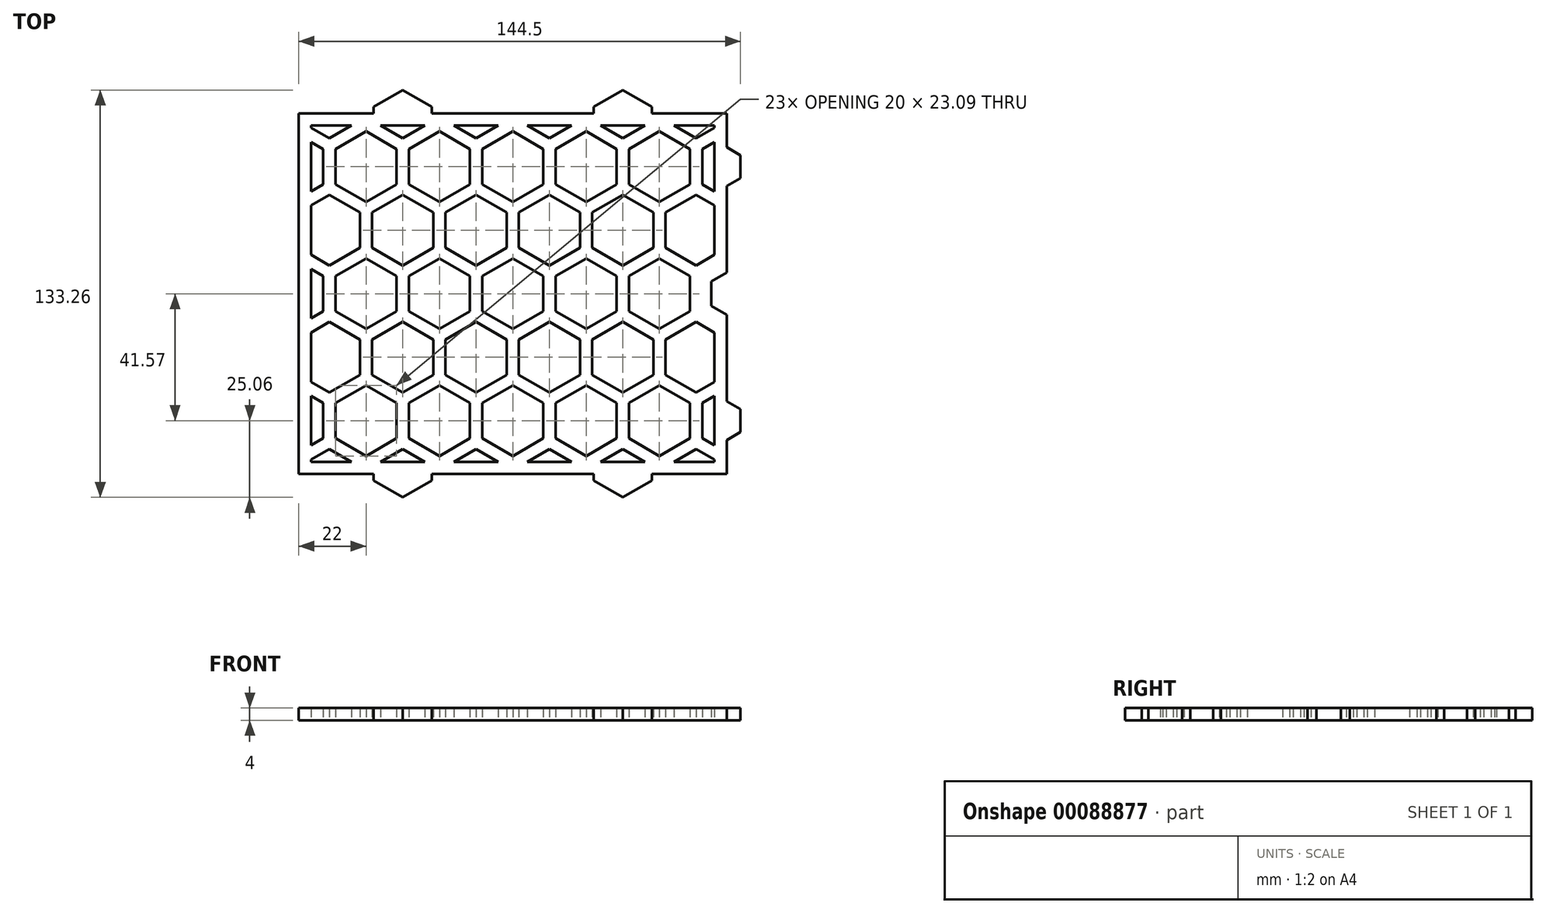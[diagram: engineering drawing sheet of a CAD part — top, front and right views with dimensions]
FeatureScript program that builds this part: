
annotation { "Feature Type Name" : "Feature", "Feature Type Description" : "" }
export const myFeature = defineFeature(function(context is Context, id is Id, definition is map)
    precondition{}
    {
        {
            var Q0;
            Q0=qCreatedBy(makeId("Top.planeOp"),FACE);
            var sketch = newSketch(context, id + "F0", { "sketchPlane" : qUnion([Q0])});
            skLineSegment(sketch, "E0.bottom", {"start": v(70, -59) * mm, "end": v(-70, -59) * mm});
            skLineSegment(sketch, "E0.top", {"start": v(70, 59) * mm, "end": v(-70, 59) * mm});
            skLineSegment(sketch, "E0.left", {"start": v(70, -59) * mm, "end": v(70, 59) * mm});
            skLineSegment(sketch, "E0.right", {"start": v(-70, -59) * mm, "end": v(-70, 59) * mm});
            skPoint(sketch, "E0.middle", {"position": v(0, 0) * mm});
            skLineSegment(sketch, "E1.0", {"start": v(-66, -55) * mm, "end": v(-66, 55) * mm});
            skLineSegment(sketch, "E1.1", {"start": v(66, -55) * mm, "end": v(-66, -55) * mm});
            skLineSegment(sketch, "E1.2", {"start": v(66, -55) * mm, "end": v(66, 55) * mm});
            skLineSegment(sketch, "E1.3", {"start": v(66, 55) * mm, "end": v(-66, 55) * mm});
            skSolve(sketch);
        }
        {
            var Q0;
            Q0=qSketchRegion(id+"F0",true);
            extrude(context, id + "F1", {"entities" : qUnion([Q0]), "depth" : 4 * mm});
        }
        {
            var Q0;
            Q0=qCreatedBy(makeId("Top.planeOp"),FACE);
            var sketch = newSketch(context, id + "F2", { "sketchPlane" : qUnion([Q0])});
            skLineSegment(sketch, "E2.0.1.1", {"start": v(-62, -47.34) * mm, "end": v(-66, -49.65) * mm});
            skLineSegment(sketch, "E2.0.1.5", {"start": v(-66, -33.49) * mm, "end": v(-62, -35.8) * mm});
            skLineSegment(sketch, "E2.0.1.13", {"start": v(-62, -35.8) * mm, "end": v(-62, -47.34) * mm});
            skLineSegment(sketch, "E2.0.2.1", {"start": v(-62, -5.77) * mm, "end": v(-66, -8.08) * mm});
            skLineSegment(sketch, "E2.0.2.5", {"start": v(-66, 8.08) * mm, "end": v(-62, 5.77) * mm});
            skLineSegment(sketch, "E2.0.2.13", {"start": v(-62, 5.77) * mm, "end": v(-62, -5.77) * mm});
            skLineSegment(sketch, "E2.0.3.1", {"start": v(-62, 35.8) * mm, "end": v(-66, 33.49) * mm});
            skLineSegment(sketch, "E2.0.3.5", {"start": v(-66, 49.65) * mm, "end": v(-62, 47.34) * mm});
            skLineSegment(sketch, "E2.0.3.13", {"start": v(-62, 47.34) * mm, "end": v(-62, 35.8) * mm});
            skLineSegment(sketch, "E2.1.0.7", {"start": v(-60, -50.8) * mm, "end": v(-52.74, -55) * mm});
            skLineSegment(sketch, "E2.1.0.8", {"start": v(-66, -54.27) * mm, "end": v(-60, -50.8) * mm});
            skCircle(sketch, "E2.1.1.0", {"center": v(-48, -41.57) * mm, "radius": 11.55 * mm, "construction": true});
            skLineSegment(sketch, "E2.1.1.1", {"start": v(-38, -47.34) * mm, "end": v(-48, -53.12) * mm});
            skLineSegment(sketch, "E2.1.1.2", {"start": v(-48, -53.12) * mm, "end": v(-58, -47.34) * mm});
            skLineSegment(sketch, "E2.1.1.3", {"start": v(-58, -47.34) * mm, "end": v(-58, -35.8) * mm});
            skLineSegment(sketch, "E2.1.1.4", {"start": v(-58, -35.8) * mm, "end": v(-48, -30.02) * mm});
            skLineSegment(sketch, "E2.1.1.5", {"start": v(-48, -30.02) * mm, "end": v(-38, -35.8) * mm});
            skLineSegment(sketch, "E2.1.1.6", {"start": v(-50, -15.01) * mm, "end": v(-50, -26.56) * mm});
            skLineSegment(sketch, "E2.1.1.7", {"start": v(-60, -9.24) * mm, "end": v(-50, -15.01) * mm});
            skLineSegment(sketch, "E2.1.1.8", {"start": v(-66, -12.7) * mm, "end": v(-60, -9.24) * mm});
            skLineSegment(sketch, "E2.1.1.10", {"start": v(-60, -32.33) * mm, "end": v(-66, -28.87) * mm});
            skLineSegment(sketch, "E2.1.1.11", {"start": v(-50, -26.56) * mm, "end": v(-60, -32.33) * mm});
            skLineSegment(sketch, "E2.1.1.13", {"start": v(-38, -35.8) * mm, "end": v(-38, -47.34) * mm});
            skCircle(sketch, "E2.1.2.0", {"center": v(-48, 0) * mm, "radius": 11.55 * mm, "construction": true});
            skLineSegment(sketch, "E2.1.2.1", {"start": v(-38, -5.77) * mm, "end": v(-48, -11.55) * mm});
            skLineSegment(sketch, "E2.1.2.2", {"start": v(-48, -11.55) * mm, "end": v(-58, -5.77) * mm});
            skLineSegment(sketch, "E2.1.2.3", {"start": v(-58, -5.77) * mm, "end": v(-58, 5.77) * mm});
            skLineSegment(sketch, "E2.1.2.4", {"start": v(-58, 5.77) * mm, "end": v(-48, 11.55) * mm});
            skLineSegment(sketch, "E2.1.2.5", {"start": v(-48, 11.55) * mm, "end": v(-38, 5.77) * mm});
            skLineSegment(sketch, "E2.1.2.6", {"start": v(-50, 26.56) * mm, "end": v(-50, 15.01) * mm});
            skLineSegment(sketch, "E2.1.2.7", {"start": v(-60, 32.33) * mm, "end": v(-50, 26.56) * mm});
            skLineSegment(sketch, "E2.1.2.8", {"start": v(-66, 28.87) * mm, "end": v(-60, 32.33) * mm});
            skLineSegment(sketch, "E2.1.2.10", {"start": v(-60, 9.24) * mm, "end": v(-66, 12.7) * mm});
            skLineSegment(sketch, "E2.1.2.11", {"start": v(-50, 15.01) * mm, "end": v(-60, 9.24) * mm});
            skLineSegment(sketch, "E2.1.2.13", {"start": v(-38, 5.77) * mm, "end": v(-38, -5.77) * mm});
            skCircle(sketch, "E2.1.3.0", {"center": v(-48, 41.57) * mm, "radius": 11.55 * mm, "construction": true});
            skLineSegment(sketch, "E2.1.3.1", {"start": v(-38, 35.8) * mm, "end": v(-48, 30.02) * mm});
            skLineSegment(sketch, "E2.1.3.2", {"start": v(-48, 30.02) * mm, "end": v(-58, 35.8) * mm});
            skLineSegment(sketch, "E2.1.3.3", {"start": v(-58, 35.8) * mm, "end": v(-58, 47.34) * mm});
            skLineSegment(sketch, "E2.1.3.4", {"start": v(-58, 47.34) * mm, "end": v(-48, 53.12) * mm});
            skLineSegment(sketch, "E2.1.3.5", {"start": v(-48, 53.12) * mm, "end": v(-38, 47.34) * mm});
            skLineSegment(sketch, "E2.1.3.10", {"start": v(-60, 50.8) * mm, "end": v(-66, 54.27) * mm});
            skLineSegment(sketch, "E2.1.3.11", {"start": v(-52.74, 55) * mm, "end": v(-60, 50.8) * mm});
            skLineSegment(sketch, "E2.1.3.13", {"start": v(-38, 47.34) * mm, "end": v(-38, 35.8) * mm});
            skLineSegment(sketch, "E2.2.0.7", {"start": v(-36, -50.8) * mm, "end": v(-28.74, -55) * mm});
            skLineSegment(sketch, "E2.2.0.8", {"start": v(-43.26, -55) * mm, "end": v(-36, -50.8) * mm});
            skCircle(sketch, "E2.2.1.0", {"center": v(-24, -41.57) * mm, "radius": 11.55 * mm, "construction": true});
            skLineSegment(sketch, "E2.2.1.1", {"start": v(-14, -47.34) * mm, "end": v(-24, -53.12) * mm});
            skLineSegment(sketch, "E2.2.1.2", {"start": v(-24, -53.12) * mm, "end": v(-34, -47.34) * mm});
            skLineSegment(sketch, "E2.2.1.3", {"start": v(-34, -47.34) * mm, "end": v(-34, -35.8) * mm});
            skLineSegment(sketch, "E2.2.1.4", {"start": v(-34, -35.8) * mm, "end": v(-24, -30.02) * mm});
            skLineSegment(sketch, "E2.2.1.5", {"start": v(-24, -30.02) * mm, "end": v(-14, -35.8) * mm});
            skLineSegment(sketch, "E2.2.1.6", {"start": v(-26, -15.01) * mm, "end": v(-26, -26.56) * mm});
            skLineSegment(sketch, "E2.2.1.7", {"start": v(-36, -9.24) * mm, "end": v(-26, -15.01) * mm});
            skLineSegment(sketch, "E2.2.1.8", {"start": v(-46, -15.01) * mm, "end": v(-36, -9.24) * mm});
            skLineSegment(sketch, "E2.2.1.9", {"start": v(-46, -26.56) * mm, "end": v(-46, -15.01) * mm});
            skLineSegment(sketch, "E2.2.1.10", {"start": v(-36, -32.33) * mm, "end": v(-46, -26.56) * mm});
            skLineSegment(sketch, "E2.2.1.11", {"start": v(-26, -26.56) * mm, "end": v(-36, -32.33) * mm});
            skCircle(sketch, "E2.2.1.12", {"center": v(-36, -20.79) * mm, "radius": 11.55 * mm, "construction": true});
            skLineSegment(sketch, "E2.2.1.13", {"start": v(-14, -35.8) * mm, "end": v(-14, -47.34) * mm});
            skCircle(sketch, "E2.2.2.0", {"center": v(-24, 0) * mm, "radius": 11.55 * mm, "construction": true});
            skLineSegment(sketch, "E2.2.2.1", {"start": v(-14, -5.77) * mm, "end": v(-24, -11.55) * mm});
            skLineSegment(sketch, "E2.2.2.2", {"start": v(-24, -11.55) * mm, "end": v(-34, -5.77) * mm});
            skLineSegment(sketch, "E2.2.2.3", {"start": v(-34, -5.77) * mm, "end": v(-34, 5.77) * mm});
            skLineSegment(sketch, "E2.2.2.4", {"start": v(-34, 5.77) * mm, "end": v(-24, 11.55) * mm});
            skLineSegment(sketch, "E2.2.2.5", {"start": v(-24, 11.55) * mm, "end": v(-14, 5.77) * mm});
            skLineSegment(sketch, "E2.2.2.6", {"start": v(-26, 26.56) * mm, "end": v(-26, 15.01) * mm});
            skLineSegment(sketch, "E2.2.2.7", {"start": v(-36, 32.33) * mm, "end": v(-26, 26.56) * mm});
            skLineSegment(sketch, "E2.2.2.8", {"start": v(-46, 26.56) * mm, "end": v(-36, 32.33) * mm});
            skLineSegment(sketch, "E2.2.2.9", {"start": v(-46, 15.01) * mm, "end": v(-46, 26.56) * mm});
            skLineSegment(sketch, "E2.2.2.10", {"start": v(-36, 9.24) * mm, "end": v(-46, 15.01) * mm});
            skLineSegment(sketch, "E2.2.2.11", {"start": v(-26, 15.01) * mm, "end": v(-36, 9.24) * mm});
            skCircle(sketch, "E2.2.2.12", {"center": v(-36, 20.78) * mm, "radius": 11.55 * mm, "construction": true});
            skLineSegment(sketch, "E2.2.2.13", {"start": v(-14, 5.77) * mm, "end": v(-14, -5.77) * mm});
            skCircle(sketch, "E2.2.3.0", {"center": v(-24, 41.57) * mm, "radius": 11.55 * mm, "construction": true});
            skLineSegment(sketch, "E2.2.3.1", {"start": v(-14, 35.8) * mm, "end": v(-24, 30.02) * mm});
            skLineSegment(sketch, "E2.2.3.2", {"start": v(-24, 30.02) * mm, "end": v(-34, 35.8) * mm});
            skLineSegment(sketch, "E2.2.3.3", {"start": v(-34, 35.8) * mm, "end": v(-34, 47.34) * mm});
            skLineSegment(sketch, "E2.2.3.4", {"start": v(-34, 47.34) * mm, "end": v(-24, 53.12) * mm});
            skLineSegment(sketch, "E2.2.3.5", {"start": v(-24, 53.12) * mm, "end": v(-14, 47.34) * mm});
            skLineSegment(sketch, "E2.2.3.10", {"start": v(-36, 50.8) * mm, "end": v(-43.26, 55) * mm});
            skLineSegment(sketch, "E2.2.3.11", {"start": v(-28.74, 55) * mm, "end": v(-36, 50.8) * mm});
            skLineSegment(sketch, "E2.2.3.13", {"start": v(-14, 47.34) * mm, "end": v(-14, 35.8) * mm});
            skLineSegment(sketch, "E2.3.0.7", {"start": v(-12, -50.8) * mm, "end": v(-4.74, -55) * mm});
            skLineSegment(sketch, "E2.3.0.8", {"start": v(-19.26, -55) * mm, "end": v(-12, -50.8) * mm});
            skCircle(sketch, "E2.3.1.0", {"center": v(0, -41.57) * mm, "radius": 11.55 * mm, "construction": true});
            skLineSegment(sketch, "E2.3.1.1", {"start": v(10, -47.34) * mm, "end": v(0, -53.12) * mm});
            skLineSegment(sketch, "E2.3.1.2", {"start": v(0, -53.12) * mm, "end": v(-10, -47.34) * mm});
            skLineSegment(sketch, "E2.3.1.3", {"start": v(-10, -47.34) * mm, "end": v(-10, -35.8) * mm});
            skLineSegment(sketch, "E2.3.1.4", {"start": v(-10, -35.8) * mm, "end": v(0, -30.02) * mm});
            skLineSegment(sketch, "E2.3.1.5", {"start": v(0, -30.02) * mm, "end": v(10, -35.8) * mm});
            skLineSegment(sketch, "E2.3.1.6", {"start": v(-2, -15.01) * mm, "end": v(-2, -26.56) * mm});
            skLineSegment(sketch, "E2.3.1.7", {"start": v(-12, -9.24) * mm, "end": v(-2, -15.01) * mm});
            skLineSegment(sketch, "E2.3.1.8", {"start": v(-22, -15.01) * mm, "end": v(-12, -9.24) * mm});
            skLineSegment(sketch, "E2.3.1.9", {"start": v(-22, -26.56) * mm, "end": v(-22, -15.01) * mm});
            skLineSegment(sketch, "E2.3.1.10", {"start": v(-12, -32.33) * mm, "end": v(-22, -26.56) * mm});
            skLineSegment(sketch, "E2.3.1.11", {"start": v(-2, -26.56) * mm, "end": v(-12, -32.33) * mm});
            skCircle(sketch, "E2.3.1.12", {"center": v(-12, -20.79) * mm, "radius": 11.55 * mm, "construction": true});
            skLineSegment(sketch, "E2.3.1.13", {"start": v(10, -35.8) * mm, "end": v(10, -47.34) * mm});
            skCircle(sketch, "E2.3.2.0", {"center": v(0, 0) * mm, "radius": 11.55 * mm, "construction": true});
            skLineSegment(sketch, "E2.3.2.1", {"start": v(10, -5.77) * mm, "end": v(0, -11.55) * mm});
            skLineSegment(sketch, "E2.3.2.2", {"start": v(0, -11.55) * mm, "end": v(-10, -5.77) * mm});
            skLineSegment(sketch, "E2.3.2.3", {"start": v(-10, -5.77) * mm, "end": v(-10, 5.77) * mm});
            skLineSegment(sketch, "E2.3.2.4", {"start": v(-10, 5.77) * mm, "end": v(0, 11.55) * mm});
            skLineSegment(sketch, "E2.3.2.5", {"start": v(0, 11.55) * mm, "end": v(10, 5.77) * mm});
            skLineSegment(sketch, "E2.3.2.6", {"start": v(-2, 26.56) * mm, "end": v(-2, 15.01) * mm});
            skLineSegment(sketch, "E2.3.2.7", {"start": v(-12, 32.33) * mm, "end": v(-2, 26.56) * mm});
            skLineSegment(sketch, "E2.3.2.8", {"start": v(-22, 26.56) * mm, "end": v(-12, 32.33) * mm});
            skLineSegment(sketch, "E2.3.2.9", {"start": v(-22, 15.01) * mm, "end": v(-22, 26.56) * mm});
            skLineSegment(sketch, "E2.3.2.10", {"start": v(-12, 9.24) * mm, "end": v(-22, 15.01) * mm});
            skLineSegment(sketch, "E2.3.2.11", {"start": v(-2, 15.01) * mm, "end": v(-12, 9.24) * mm});
            skCircle(sketch, "E2.3.2.12", {"center": v(-12, 20.78) * mm, "radius": 11.55 * mm, "construction": true});
            skLineSegment(sketch, "E2.3.2.13", {"start": v(10, 5.77) * mm, "end": v(10, -5.77) * mm});
            skCircle(sketch, "E2.3.3.0", {"center": v(0, 41.57) * mm, "radius": 11.55 * mm, "construction": true});
            skLineSegment(sketch, "E2.3.3.1", {"start": v(10, 35.8) * mm, "end": v(0, 30.02) * mm});
            skLineSegment(sketch, "E2.3.3.2", {"start": v(0, 30.02) * mm, "end": v(-10, 35.8) * mm});
            skLineSegment(sketch, "E2.3.3.3", {"start": v(-10, 35.8) * mm, "end": v(-10, 47.34) * mm});
            skLineSegment(sketch, "E2.3.3.4", {"start": v(-10, 47.34) * mm, "end": v(0, 53.12) * mm});
            skLineSegment(sketch, "E2.3.3.5", {"start": v(0, 53.12) * mm, "end": v(10, 47.34) * mm});
            skLineSegment(sketch, "E2.3.3.10", {"start": v(-12, 50.8) * mm, "end": v(-19.26, 55) * mm});
            skLineSegment(sketch, "E2.3.3.11", {"start": v(-4.74, 55) * mm, "end": v(-12, 50.8) * mm});
            skLineSegment(sketch, "E2.3.3.13", {"start": v(10, 47.34) * mm, "end": v(10, 35.8) * mm});
            skLineSegment(sketch, "E2.4.0.7", {"start": v(12, -50.8) * mm, "end": v(19.26, -55) * mm});
            skLineSegment(sketch, "E2.4.0.8", {"start": v(4.74, -55) * mm, "end": v(12, -50.8) * mm});
            skCircle(sketch, "E2.4.1.0", {"center": v(24, -41.57) * mm, "radius": 11.55 * mm, "construction": true});
            skLineSegment(sketch, "E2.4.1.1", {"start": v(34, -47.34) * mm, "end": v(24, -53.12) * mm});
            skLineSegment(sketch, "E2.4.1.2", {"start": v(24, -53.12) * mm, "end": v(14, -47.34) * mm});
            skLineSegment(sketch, "E2.4.1.3", {"start": v(14, -47.34) * mm, "end": v(14, -35.8) * mm});
            skLineSegment(sketch, "E2.4.1.4", {"start": v(14, -35.8) * mm, "end": v(24, -30.02) * mm});
            skLineSegment(sketch, "E2.4.1.5", {"start": v(24, -30.02) * mm, "end": v(34, -35.8) * mm});
            skLineSegment(sketch, "E2.4.1.6", {"start": v(22, -15.01) * mm, "end": v(22, -26.56) * mm});
            skLineSegment(sketch, "E2.4.1.7", {"start": v(12, -9.24) * mm, "end": v(22, -15.01) * mm});
            skLineSegment(sketch, "E2.4.1.8", {"start": v(2, -15.01) * mm, "end": v(12, -9.24) * mm});
            skLineSegment(sketch, "E2.4.1.9", {"start": v(2, -26.56) * mm, "end": v(2, -15.01) * mm});
            skLineSegment(sketch, "E2.4.1.10", {"start": v(12, -32.33) * mm, "end": v(2, -26.56) * mm});
            skLineSegment(sketch, "E2.4.1.11", {"start": v(22, -26.56) * mm, "end": v(12, -32.33) * mm});
            skCircle(sketch, "E2.4.1.12", {"center": v(12, -20.79) * mm, "radius": 11.55 * mm, "construction": true});
            skLineSegment(sketch, "E2.4.1.13", {"start": v(34, -35.8) * mm, "end": v(34, -47.34) * mm});
            skCircle(sketch, "E2.4.2.0", {"center": v(24, 0) * mm, "radius": 11.55 * mm, "construction": true});
            skLineSegment(sketch, "E2.4.2.1", {"start": v(34, -5.77) * mm, "end": v(24, -11.55) * mm});
            skLineSegment(sketch, "E2.4.2.2", {"start": v(24, -11.55) * mm, "end": v(14, -5.77) * mm});
            skLineSegment(sketch, "E2.4.2.3", {"start": v(14, -5.77) * mm, "end": v(14, 5.77) * mm});
            skLineSegment(sketch, "E2.4.2.4", {"start": v(14, 5.77) * mm, "end": v(24, 11.55) * mm});
            skLineSegment(sketch, "E2.4.2.5", {"start": v(24, 11.55) * mm, "end": v(34, 5.77) * mm});
            skLineSegment(sketch, "E2.4.2.6", {"start": v(22, 26.56) * mm, "end": v(22, 15.01) * mm});
            skLineSegment(sketch, "E2.4.2.7", {"start": v(12, 32.33) * mm, "end": v(22, 26.56) * mm});
            skLineSegment(sketch, "E2.4.2.8", {"start": v(2, 26.56) * mm, "end": v(12, 32.33) * mm});
            skLineSegment(sketch, "E2.4.2.9", {"start": v(2, 15.01) * mm, "end": v(2, 26.56) * mm});
            skLineSegment(sketch, "E2.4.2.10", {"start": v(12, 9.24) * mm, "end": v(2, 15.01) * mm});
            skLineSegment(sketch, "E2.4.2.11", {"start": v(22, 15.01) * mm, "end": v(12, 9.24) * mm});
            skCircle(sketch, "E2.4.2.12", {"center": v(12, 20.78) * mm, "radius": 11.55 * mm, "construction": true});
            skLineSegment(sketch, "E2.4.2.13", {"start": v(34, 5.77) * mm, "end": v(34, -5.77) * mm});
            skCircle(sketch, "E2.4.3.0", {"center": v(24, 41.57) * mm, "radius": 11.55 * mm, "construction": true});
            skLineSegment(sketch, "E2.4.3.1", {"start": v(34, 35.8) * mm, "end": v(24, 30.02) * mm});
            skLineSegment(sketch, "E2.4.3.2", {"start": v(24, 30.02) * mm, "end": v(14, 35.8) * mm});
            skLineSegment(sketch, "E2.4.3.3", {"start": v(14, 35.8) * mm, "end": v(14, 47.34) * mm});
            skLineSegment(sketch, "E2.4.3.4", {"start": v(14, 47.34) * mm, "end": v(24, 53.12) * mm});
            skLineSegment(sketch, "E2.4.3.5", {"start": v(24, 53.12) * mm, "end": v(34, 47.34) * mm});
            skLineSegment(sketch, "E2.4.3.10", {"start": v(12, 50.8) * mm, "end": v(4.74, 55) * mm});
            skLineSegment(sketch, "E2.4.3.11", {"start": v(19.26, 55) * mm, "end": v(12, 50.8) * mm});
            skLineSegment(sketch, "E2.4.3.13", {"start": v(34, 47.34) * mm, "end": v(34, 35.8) * mm});
            skLineSegment(sketch, "E2.5.0.7", {"start": v(36, -50.8) * mm, "end": v(43.26, -55) * mm});
            skLineSegment(sketch, "E2.5.0.8", {"start": v(28.74, -55) * mm, "end": v(36, -50.8) * mm});
            skCircle(sketch, "E2.5.1.0", {"center": v(48, -41.57) * mm, "radius": 11.55 * mm, "construction": true});
            skLineSegment(sketch, "E2.5.1.1", {"start": v(58, -47.34) * mm, "end": v(48, -53.12) * mm});
            skLineSegment(sketch, "E2.5.1.2", {"start": v(48, -53.12) * mm, "end": v(38, -47.34) * mm});
            skLineSegment(sketch, "E2.5.1.3", {"start": v(38, -47.34) * mm, "end": v(38, -35.8) * mm});
            skLineSegment(sketch, "E2.5.1.4", {"start": v(38, -35.8) * mm, "end": v(48, -30.02) * mm});
            skLineSegment(sketch, "E2.5.1.5", {"start": v(48, -30.02) * mm, "end": v(58, -35.8) * mm});
            skLineSegment(sketch, "E2.5.1.6", {"start": v(46, -15.01) * mm, "end": v(46, -26.56) * mm});
            skLineSegment(sketch, "E2.5.1.7", {"start": v(36, -9.24) * mm, "end": v(46, -15.01) * mm});
            skLineSegment(sketch, "E2.5.1.8", {"start": v(26, -15.01) * mm, "end": v(36, -9.24) * mm});
            skLineSegment(sketch, "E2.5.1.9", {"start": v(26, -26.56) * mm, "end": v(26, -15.01) * mm});
            skLineSegment(sketch, "E2.5.1.10", {"start": v(36, -32.33) * mm, "end": v(26, -26.56) * mm});
            skLineSegment(sketch, "E2.5.1.11", {"start": v(46, -26.56) * mm, "end": v(36, -32.33) * mm});
            skCircle(sketch, "E2.5.1.12", {"center": v(36, -20.79) * mm, "radius": 11.55 * mm, "construction": true});
            skLineSegment(sketch, "E2.5.1.13", {"start": v(58, -35.8) * mm, "end": v(58, -47.34) * mm});
            skCircle(sketch, "E2.5.2.0", {"center": v(48, 0) * mm, "radius": 11.55 * mm, "construction": true});
            skLineSegment(sketch, "E2.5.2.1", {"start": v(58, -5.77) * mm, "end": v(48, -11.55) * mm});
            skLineSegment(sketch, "E2.5.2.2", {"start": v(48, -11.55) * mm, "end": v(38, -5.77) * mm});
            skLineSegment(sketch, "E2.5.2.3", {"start": v(38, -5.77) * mm, "end": v(38, 5.77) * mm});
            skLineSegment(sketch, "E2.5.2.4", {"start": v(38, 5.77) * mm, "end": v(48, 11.55) * mm});
            skLineSegment(sketch, "E2.5.2.5", {"start": v(48, 11.55) * mm, "end": v(58, 5.77) * mm});
            skLineSegment(sketch, "E2.5.2.6", {"start": v(46, 26.56) * mm, "end": v(46, 15.01) * mm});
            skLineSegment(sketch, "E2.5.2.7", {"start": v(36, 32.33) * mm, "end": v(46, 26.56) * mm});
            skLineSegment(sketch, "E2.5.2.8", {"start": v(26, 26.56) * mm, "end": v(36, 32.33) * mm});
            skLineSegment(sketch, "E2.5.2.9", {"start": v(26, 15.01) * mm, "end": v(26, 26.56) * mm});
            skLineSegment(sketch, "E2.5.2.10", {"start": v(36, 9.24) * mm, "end": v(26, 15.01) * mm});
            skLineSegment(sketch, "E2.5.2.11", {"start": v(46, 15.01) * mm, "end": v(36, 9.24) * mm});
            skCircle(sketch, "E2.5.2.12", {"center": v(36, 20.78) * mm, "radius": 11.55 * mm, "construction": true});
            skLineSegment(sketch, "E2.5.2.13", {"start": v(58, 5.77) * mm, "end": v(58, -5.77) * mm});
            skCircle(sketch, "E2.5.3.0", {"center": v(48, 41.57) * mm, "radius": 11.55 * mm, "construction": true});
            skLineSegment(sketch, "E2.5.3.1", {"start": v(58, 35.8) * mm, "end": v(48, 30.02) * mm});
            skLineSegment(sketch, "E2.5.3.2", {"start": v(48, 30.02) * mm, "end": v(38, 35.8) * mm});
            skLineSegment(sketch, "E2.5.3.3", {"start": v(38, 35.8) * mm, "end": v(38, 47.34) * mm});
            skLineSegment(sketch, "E2.5.3.4", {"start": v(38, 47.34) * mm, "end": v(48, 53.12) * mm});
            skLineSegment(sketch, "E2.5.3.5", {"start": v(48, 53.12) * mm, "end": v(58, 47.34) * mm});
            skLineSegment(sketch, "E2.5.3.10", {"start": v(36, 50.8) * mm, "end": v(28.74, 55) * mm});
            skLineSegment(sketch, "E2.5.3.11", {"start": v(43.26, 55) * mm, "end": v(36, 50.8) * mm});
            skLineSegment(sketch, "E2.5.3.13", {"start": v(58, 47.34) * mm, "end": v(58, 35.8) * mm});
            skLineSegment(sketch, "E2.6.0.7", {"start": v(60, -50.8) * mm, "end": v(66, -54.27) * mm});
            skLineSegment(sketch, "E2.6.0.8", {"start": v(52.74, -55) * mm, "end": v(60, -50.8) * mm});
            skLineSegment(sketch, "E2.6.1.2", {"start": v(66, -49.65) * mm, "end": v(62, -47.34) * mm});
            skLineSegment(sketch, "E2.6.1.3", {"start": v(62, -47.34) * mm, "end": v(62, -35.8) * mm});
            skLineSegment(sketch, "E2.6.1.4", {"start": v(62, -35.8) * mm, "end": v(66, -33.49) * mm});
            skLineSegment(sketch, "E2.6.1.7", {"start": v(60, -9.24) * mm, "end": v(66, -12.7) * mm});
            skLineSegment(sketch, "E2.6.1.8", {"start": v(50, -15.01) * mm, "end": v(60, -9.24) * mm});
            skLineSegment(sketch, "E2.6.1.9", {"start": v(50, -26.56) * mm, "end": v(50, -15.01) * mm});
            skLineSegment(sketch, "E2.6.1.10", {"start": v(60, -32.33) * mm, "end": v(50, -26.56) * mm});
            skLineSegment(sketch, "E2.6.1.11", {"start": v(66, -28.87) * mm, "end": v(60, -32.33) * mm});
            skLineSegment(sketch, "E2.6.2.2", {"start": v(66, -8.08) * mm, "end": v(62, -5.77) * mm});
            skLineSegment(sketch, "E2.6.2.3", {"start": v(62, -5.77) * mm, "end": v(62, 5.77) * mm});
            skLineSegment(sketch, "E2.6.2.4", {"start": v(62, 5.77) * mm, "end": v(66, 8.08) * mm});
            skLineSegment(sketch, "E2.6.2.7", {"start": v(60, 32.33) * mm, "end": v(66, 28.87) * mm});
            skLineSegment(sketch, "E2.6.2.8", {"start": v(50, 26.56) * mm, "end": v(60, 32.33) * mm});
            skLineSegment(sketch, "E2.6.2.9", {"start": v(50, 15.01) * mm, "end": v(50, 26.56) * mm});
            skLineSegment(sketch, "E2.6.2.10", {"start": v(60, 9.24) * mm, "end": v(50, 15.01) * mm});
            skLineSegment(sketch, "E2.6.2.11", {"start": v(66, 12.7) * mm, "end": v(60, 9.24) * mm});
            skLineSegment(sketch, "E2.6.3.2", {"start": v(66, 33.49) * mm, "end": v(62, 35.8) * mm});
            skLineSegment(sketch, "E2.6.3.3", {"start": v(62, 35.8) * mm, "end": v(62, 47.34) * mm});
            skLineSegment(sketch, "E2.6.3.4", {"start": v(62, 47.34) * mm, "end": v(66, 49.65) * mm});
            skLineSegment(sketch, "E2.6.3.10", {"start": v(60, 50.8) * mm, "end": v(52.74, 55) * mm});
            skLineSegment(sketch, "E2.6.3.11", {"start": v(66, 54.27) * mm, "end": v(60, 50.8) * mm});
            skLineSegment(sketch, "E3.0", {"start": v(-66, -55) * mm, "end": v(-66, -54.27) * mm});
            skLineSegment(sketch, "E3.1", {"start": v(66, 55) * mm, "end": v(52.74, 55) * mm});
            skLineSegment(sketch, "E3.2", {"start": v(66, -55) * mm, "end": v(66, -54.27) * mm});
            skLineSegment(sketch, "E3.3", {"start": v(66, -55) * mm, "end": v(52.74, -55) * mm});
            skLineSegment(sketch, "E4.trimOffspring", {"start": v(-66, 54.27) * mm, "end": v(-66, 55) * mm});
            skLineSegment(sketch, "E5.trimOffspring", {"start": v(-66, 33.49) * mm, "end": v(-66, 49.65) * mm});
            skLineSegment(sketch, "E6.trimOffspring", {"start": v(-66, 12.7) * mm, "end": v(-66, 28.87) * mm});
            skLineSegment(sketch, "E7.trimOffspring", {"start": v(-52.74, 55) * mm, "end": v(-66, 55) * mm});
            skLineSegment(sketch, "E8.trimOffspring", {"start": v(-28.74, 55) * mm, "end": v(-43.26, 55) * mm});
            skLineSegment(sketch, "E9.trimOffspring", {"start": v(-4.74, 55) * mm, "end": v(-19.26, 55) * mm});
            skLineSegment(sketch, "E10.trimOffspring", {"start": v(19.26, 55) * mm, "end": v(4.74, 55) * mm});
            skLineSegment(sketch, "E11.trimOffspring", {"start": v(43.26, 55) * mm, "end": v(28.74, 55) * mm});
            skLineSegment(sketch, "E12.trimOffspring", {"start": v(66, 54.27) * mm, "end": v(66, 55) * mm});
            skLineSegment(sketch, "E13.trimOffspring", {"start": v(66, 33.49) * mm, "end": v(66, 49.65) * mm});
            skLineSegment(sketch, "E14.trimOffspring", {"start": v(66, 12.7) * mm, "end": v(66, 28.87) * mm});
            skLineSegment(sketch, "E15.trimOffspring", {"start": v(66, -8.08) * mm, "end": v(66, 8.08) * mm});
            skLineSegment(sketch, "E16.trimOffspring", {"start": v(66, -28.87) * mm, "end": v(66, -12.7) * mm});
            skLineSegment(sketch, "E17.trimOffspring", {"start": v(66, -49.65) * mm, "end": v(66, -33.49) * mm});
            skLineSegment(sketch, "E18.trimOffspring", {"start": v(43.26, -55) * mm, "end": v(28.74, -55) * mm});
            skLineSegment(sketch, "E19.trimOffspring", {"start": v(19.26, -55) * mm, "end": v(4.74, -55) * mm});
            skLineSegment(sketch, "E20.trimOffspring", {"start": v(-4.74, -55) * mm, "end": v(-19.26, -55) * mm});
            skLineSegment(sketch, "E21.trimOffspring", {"start": v(-28.74, -55) * mm, "end": v(-43.26, -55) * mm});
            skLineSegment(sketch, "E22.trimOffspring", {"start": v(-52.74, -55) * mm, "end": v(-66, -55) * mm});
            skLineSegment(sketch, "E23.trimOffspring", {"start": v(-66, -49.65) * mm, "end": v(-66, -33.49) * mm});
            skLineSegment(sketch, "E24.trimOffspring", {"start": v(-66, -28.87) * mm, "end": v(-66, -12.7) * mm});
            skLineSegment(sketch, "E25.trimOffspring", {"start": v(-66, -8.08) * mm, "end": v(-66, 8.08) * mm});
            skLineSegment(sketch, "E26.0", {"start": v(-70, -59) * mm, "end": v(-70, 59) * mm});
            skLineSegment(sketch, "E26.1", {"start": v(70, 59) * mm, "end": v(-70, 59) * mm});
            skLineSegment(sketch, "E26.2", {"start": v(70, -59) * mm, "end": v(70, 59) * mm});
            skLineSegment(sketch, "E26.3", {"start": v(70, -59) * mm, "end": v(-70, -59) * mm});
            skSolve(sketch);
        }
        {
            var Q0;
            Q0=qSketchRegion(id+"F2",true);
            var Q1;
            Q1=makeQuery(id+"F1.opExtrude","CAP_FACE",FACE,{"disambiguationData":[OSD([sQuery(id+"F0.wireOp",EDGE,"E0.bottom"),sQuery(id+"F0.wireOp",EDGE,"E0.top"),sQuery(id+"F0.wireOp",EDGE,"E0.left"),sQuery(id+"F0.wireOp",EDGE,"E0.right"),sQuery(id+"F0.wireOp",EDGE,"E1.0"),sQuery(id+"F0.wireOp",EDGE,"E1.1"),sQuery(id+"F0.wireOp",EDGE,"E1.2"),sQuery(id+"F0.wireOp",EDGE,"E1.3")])],"isStart":false});
            extrude(context, id + "F3", {"entities" : qUnion([Q0]), "operationType" : NewBodyOperationType.ADD, "endBound" : BoundingType.UP_TO_SURFACE, "endBoundEntityFace" : qUnion([Q1]), "depth" : 4 * mm});
        }
        {
            var Q0;
            Q0=qCreatedBy(makeId("Top.planeOp"),FACE);
            var sketch = newSketch(context, id + "F4", { "sketchPlane" : qUnion([Q0])});
            skCircle(sketch, "E27.cCircle", {"center": v(68, 41.57) * mm, "radius": 11.55 * mm, "construction": true});
            skLineSegment(sketch, "E27.0", {"start": v(78, 35.8) * mm, "end": v(70, 31.18) * mm, "construction": true});
            skLineSegment(sketch, "E27.4", {"start": v(70, 51.96) * mm, "end": v(78, 47.34) * mm, "construction": true});
            skLineSegment(sketch, "E27.5", {"start": v(78, 47.34) * mm, "end": v(78, 35.8) * mm, "construction": true});
            skCircle(sketch, "E28.cCircle", {"center": v(68, -41.57) * mm, "radius": 11.55 * mm, "construction": true});
            skLineSegment(sketch, "E28.3", {"start": v(70, -31.18) * mm, "end": v(78, -35.8) * mm, "construction": true});
            skLineSegment(sketch, "E28.4", {"start": v(78, -35.8) * mm, "end": v(78, -47.34) * mm, "construction": true});
            skLineSegment(sketch, "E28.5", {"start": v(78, -47.34) * mm, "end": v(70, -51.96) * mm, "construction": true});
            skLineSegment(sketch, "E29.0", {"start": v(70, -59) * mm, "end": v(70, 59) * mm});
            skPoint(sketch, "E30.orphan", {"position": v(68, -30.02) * mm});
            skLineSegment(sketch, "E31.0", {"start": v(74.5, 37.82) * mm, "end": v(68.25, 34.2) * mm});
            skLineSegment(sketch, "E31.1", {"start": v(74.5, 45.32) * mm, "end": v(74.5, 37.82) * mm});
            skLineSegment(sketch, "E31.2", {"start": v(68.25, 48.93) * mm, "end": v(74.5, 45.32) * mm});
            skLineSegment(sketch, "E32.0", {"start": v(74.5, -45.32) * mm, "end": v(68.25, -48.93) * mm});
            skLineSegment(sketch, "E32.1", {"start": v(74.5, -37.82) * mm, "end": v(74.5, -45.32) * mm});
            skLineSegment(sketch, "E32.2", {"start": v(68.25, -34.2) * mm, "end": v(74.5, -37.82) * mm});
            skSolve(sketch);
        }
        {
            var Q0;
            Q0=qSketchRegion(id+"F4",true);
            var Q1;
            Q1=makeQuery(id+"F3.boolean.opBoolean","MERGE",FACE,{"derivedFrom":[makeQuery(id+"F1.opExtrude","CAP_FACE",FACE,{"disambiguationData":[OSD([sQuery(id+"F0.wireOp",EDGE,"E0.bottom"),sQuery(id+"F0.wireOp",EDGE,"E0.top"),sQuery(id+"F0.wireOp",EDGE,"E0.left"),sQuery(id+"F0.wireOp",EDGE,"E0.right"),sQuery(id+"F0.wireOp",EDGE,"E1.0"),sQuery(id+"F0.wireOp",EDGE,"E1.1"),sQuery(id+"F0.wireOp",EDGE,"E1.2"),sQuery(id+"F0.wireOp",EDGE,"E1.3")])],"isStart":false}),makeQuery(id+"F3.opExtrude","CAP_FACE",FACE,{"disambiguationData":[OSD([sQuery(id+"F2.wireOp",EDGE,"E2.0.1.1"),sQuery(id+"F2.wireOp",EDGE,"E2.0.1.5"),sQuery(id+"F2.wireOp",EDGE,"E2.0.1.13"),sQuery(id+"F2.wireOp",EDGE,"E2.0.2.1"),sQuery(id+"F2.wireOp",EDGE,"E2.0.2.5"),sQuery(id+"F2.wireOp",EDGE,"E2.0.2.13"),sQuery(id+"F2.wireOp",EDGE,"E2.0.3.1"),sQuery(id+"F2.wireOp",EDGE,"E2.0.3.5"),sQuery(id+"F2.wireOp",EDGE,"E2.0.3.13"),sQuery(id+"F2.wireOp",EDGE,"E2.1.0.7"),sQuery(id+"F2.wireOp",EDGE,"E2.1.0.8"),sQuery(id+"F2.wireOp",EDGE,"E2.1.1.1"),sQuery(id+"F2.wireOp",EDGE,"E2.1.1.2"),sQuery(id+"F2.wireOp",EDGE,"E2.1.1.3"),sQuery(id+"F2.wireOp",EDGE,"E2.1.1.4"),sQuery(id+"F2.wireOp",EDGE,"E2.1.1.5"),sQuery(id+"F2.wireOp",EDGE,"E2.1.1.6"),sQuery(id+"F2.wireOp",EDGE,"E2.1.1.7"),sQuery(id+"F2.wireOp",EDGE,"E2.1.1.8"),sQuery(id+"F2.wireOp",EDGE,"E2.1.1.10"),sQuery(id+"F2.wireOp",EDGE,"E2.1.1.11"),sQuery(id+"F2.wireOp",EDGE,"E2.1.1.13"),sQuery(id+"F2.wireOp",EDGE,"E2.1.2.1"),sQuery(id+"F2.wireOp",EDGE,"E2.1.2.2"),sQuery(id+"F2.wireOp",EDGE,"E2.1.2.3"),sQuery(id+"F2.wireOp",EDGE,"E2.1.2.4"),sQuery(id+"F2.wireOp",EDGE,"E2.1.2.5"),sQuery(id+"F2.wireOp",EDGE,"E2.1.2.6"),sQuery(id+"F2.wireOp",EDGE,"E2.1.2.7"),sQuery(id+"F2.wireOp",EDGE,"E2.1.2.8"),sQuery(id+"F2.wireOp",EDGE,"E2.1.2.10"),sQuery(id+"F2.wireOp",EDGE,"E2.1.2.11"),sQuery(id+"F2.wireOp",EDGE,"E2.1.2.13"),sQuery(id+"F2.wireOp",EDGE,"E2.1.3.1"),sQuery(id+"F2.wireOp",EDGE,"E2.1.3.2"),sQuery(id+"F2.wireOp",EDGE,"E2.1.3.3"),sQuery(id+"F2.wireOp",EDGE,"E2.1.3.4"),sQuery(id+"F2.wireOp",EDGE,"E2.1.3.5"),sQuery(id+"F2.wireOp",EDGE,"E2.1.3.10"),sQuery(id+"F2.wireOp",EDGE,"E2.1.3.11"),sQuery(id+"F2.wireOp",EDGE,"E2.1.3.13"),sQuery(id+"F2.wireOp",EDGE,"E2.2.0.7"),sQuery(id+"F2.wireOp",EDGE,"E2.2.0.8"),sQuery(id+"F2.wireOp",EDGE,"E2.2.1.1"),sQuery(id+"F2.wireOp",EDGE,"E2.2.1.2"),sQuery(id+"F2.wireOp",EDGE,"E2.2.1.3"),sQuery(id+"F2.wireOp",EDGE,"E2.2.1.4"),sQuery(id+"F2.wireOp",EDGE,"E2.2.1.5"),sQuery(id+"F2.wireOp",EDGE,"E2.2.1.6"),sQuery(id+"F2.wireOp",EDGE,"E2.2.1.7"),sQuery(id+"F2.wireOp",EDGE,"E2.2.1.8"),sQuery(id+"F2.wireOp",EDGE,"E2.2.1.9"),sQuery(id+"F2.wireOp",EDGE,"E2.2.1.10"),sQuery(id+"F2.wireOp",EDGE,"E2.2.1.11"),sQuery(id+"F2.wireOp",EDGE,"E2.2.1.13"),sQuery(id+"F2.wireOp",EDGE,"E2.2.2.1"),sQuery(id+"F2.wireOp",EDGE,"E2.2.2.2"),sQuery(id+"F2.wireOp",EDGE,"E2.2.2.3"),sQuery(id+"F2.wireOp",EDGE,"E2.2.2.4"),sQuery(id+"F2.wireOp",EDGE,"E2.2.2.5"),sQuery(id+"F2.wireOp",EDGE,"E2.2.2.6"),sQuery(id+"F2.wireOp",EDGE,"E2.2.2.7"),sQuery(id+"F2.wireOp",EDGE,"E2.2.2.8"),sQuery(id+"F2.wireOp",EDGE,"E2.2.2.9"),sQuery(id+"F2.wireOp",EDGE,"E2.2.2.10"),sQuery(id+"F2.wireOp",EDGE,"E2.2.2.11"),sQuery(id+"F2.wireOp",EDGE,"E2.2.2.13"),sQuery(id+"F2.wireOp",EDGE,"E2.2.3.1"),sQuery(id+"F2.wireOp",EDGE,"E2.2.3.2"),sQuery(id+"F2.wireOp",EDGE,"E2.2.3.3"),sQuery(id+"F2.wireOp",EDGE,"E2.2.3.4"),sQuery(id+"F2.wireOp",EDGE,"E2.2.3.5"),sQuery(id+"F2.wireOp",EDGE,"E2.2.3.10"),sQuery(id+"F2.wireOp",EDGE,"E2.2.3.11"),sQuery(id+"F2.wireOp",EDGE,"E2.2.3.13"),sQuery(id+"F2.wireOp",EDGE,"E2.3.0.7"),sQuery(id+"F2.wireOp",EDGE,"E2.3.0.8"),sQuery(id+"F2.wireOp",EDGE,"E2.3.1.1"),sQuery(id+"F2.wireOp",EDGE,"E2.3.1.2"),sQuery(id+"F2.wireOp",EDGE,"E2.3.1.3"),sQuery(id+"F2.wireOp",EDGE,"E2.3.1.4"),sQuery(id+"F2.wireOp",EDGE,"E2.3.1.5"),sQuery(id+"F2.wireOp",EDGE,"E2.3.1.6"),sQuery(id+"F2.wireOp",EDGE,"E2.3.1.7"),sQuery(id+"F2.wireOp",EDGE,"E2.3.1.8"),sQuery(id+"F2.wireOp",EDGE,"E2.3.1.9"),sQuery(id+"F2.wireOp",EDGE,"E2.3.1.10"),sQuery(id+"F2.wireOp",EDGE,"E2.3.1.11"),sQuery(id+"F2.wireOp",EDGE,"E2.3.1.13"),sQuery(id+"F2.wireOp",EDGE,"E2.3.2.1"),sQuery(id+"F2.wireOp",EDGE,"E2.3.2.2"),sQuery(id+"F2.wireOp",EDGE,"E2.3.2.3"),sQuery(id+"F2.wireOp",EDGE,"E2.3.2.4"),sQuery(id+"F2.wireOp",EDGE,"E2.3.2.5"),sQuery(id+"F2.wireOp",EDGE,"E2.3.2.6"),sQuery(id+"F2.wireOp",EDGE,"E2.3.2.7"),sQuery(id+"F2.wireOp",EDGE,"E2.3.2.8"),sQuery(id+"F2.wireOp",EDGE,"E2.3.2.9"),sQuery(id+"F2.wireOp",EDGE,"E2.3.2.10"),sQuery(id+"F2.wireOp",EDGE,"E2.3.2.11"),sQuery(id+"F2.wireOp",EDGE,"E2.3.2.13"),sQuery(id+"F2.wireOp",EDGE,"E2.3.3.1"),sQuery(id+"F2.wireOp",EDGE,"E2.3.3.2"),sQuery(id+"F2.wireOp",EDGE,"E2.3.3.3"),sQuery(id+"F2.wireOp",EDGE,"E2.3.3.4"),sQuery(id+"F2.wireOp",EDGE,"E2.3.3.5"),sQuery(id+"F2.wireOp",EDGE,"E2.3.3.10"),sQuery(id+"F2.wireOp",EDGE,"E2.3.3.11"),sQuery(id+"F2.wireOp",EDGE,"E2.3.3.13"),sQuery(id+"F2.wireOp",EDGE,"E2.4.0.7"),sQuery(id+"F2.wireOp",EDGE,"E2.4.0.8"),sQuery(id+"F2.wireOp",EDGE,"E2.4.1.1"),sQuery(id+"F2.wireOp",EDGE,"E2.4.1.2"),sQuery(id+"F2.wireOp",EDGE,"E2.4.1.3"),sQuery(id+"F2.wireOp",EDGE,"E2.4.1.4"),sQuery(id+"F2.wireOp",EDGE,"E2.4.1.5"),sQuery(id+"F2.wireOp",EDGE,"E2.4.1.6"),sQuery(id+"F2.wireOp",EDGE,"E2.4.1.7"),sQuery(id+"F2.wireOp",EDGE,"E2.4.1.8"),sQuery(id+"F2.wireOp",EDGE,"E2.4.1.9"),sQuery(id+"F2.wireOp",EDGE,"E2.4.1.10"),sQuery(id+"F2.wireOp",EDGE,"E2.4.1.11"),sQuery(id+"F2.wireOp",EDGE,"E2.4.1.13"),sQuery(id+"F2.wireOp",EDGE,"E2.4.2.1"),sQuery(id+"F2.wireOp",EDGE,"E2.4.2.2"),sQuery(id+"F2.wireOp",EDGE,"E2.4.2.3"),sQuery(id+"F2.wireOp",EDGE,"E2.4.2.4"),sQuery(id+"F2.wireOp",EDGE,"E2.4.2.5"),sQuery(id+"F2.wireOp",EDGE,"E2.4.2.6"),sQuery(id+"F2.wireOp",EDGE,"E2.4.2.7"),sQuery(id+"F2.wireOp",EDGE,"E2.4.2.8"),sQuery(id+"F2.wireOp",EDGE,"E2.4.2.9"),sQuery(id+"F2.wireOp",EDGE,"E2.4.2.10"),sQuery(id+"F2.wireOp",EDGE,"E2.4.2.11"),sQuery(id+"F2.wireOp",EDGE,"E2.4.2.13"),sQuery(id+"F2.wireOp",EDGE,"E2.4.3.1"),sQuery(id+"F2.wireOp",EDGE,"E2.4.3.2"),sQuery(id+"F2.wireOp",EDGE,"E2.4.3.3"),sQuery(id+"F2.wireOp",EDGE,"E2.4.3.4"),sQuery(id+"F2.wireOp",EDGE,"E2.4.3.5"),sQuery(id+"F2.wireOp",EDGE,"E2.4.3.10"),sQuery(id+"F2.wireOp",EDGE,"E2.4.3.11"),sQuery(id+"F2.wireOp",EDGE,"E2.4.3.13"),sQuery(id+"F2.wireOp",EDGE,"E2.5.0.7"),sQuery(id+"F2.wireOp",EDGE,"E2.5.0.8"),sQuery(id+"F2.wireOp",EDGE,"E2.5.1.1"),sQuery(id+"F2.wireOp",EDGE,"E2.5.1.2"),sQuery(id+"F2.wireOp",EDGE,"E2.5.1.3"),sQuery(id+"F2.wireOp",EDGE,"E2.5.1.4"),sQuery(id+"F2.wireOp",EDGE,"E2.5.1.5"),sQuery(id+"F2.wireOp",EDGE,"E2.5.1.6"),sQuery(id+"F2.wireOp",EDGE,"E2.5.1.7"),sQuery(id+"F2.wireOp",EDGE,"E2.5.1.8"),sQuery(id+"F2.wireOp",EDGE,"E2.5.1.9"),sQuery(id+"F2.wireOp",EDGE,"E2.5.1.10"),sQuery(id+"F2.wireOp",EDGE,"E2.5.1.11"),sQuery(id+"F2.wireOp",EDGE,"E2.5.1.13"),sQuery(id+"F2.wireOp",EDGE,"E2.5.2.1"),sQuery(id+"F2.wireOp",EDGE,"E2.5.2.2"),sQuery(id+"F2.wireOp",EDGE,"E2.5.2.3"),sQuery(id+"F2.wireOp",EDGE,"E2.5.2.4"),sQuery(id+"F2.wireOp",EDGE,"E2.5.2.5"),sQuery(id+"F2.wireOp",EDGE,"E2.5.2.6"),sQuery(id+"F2.wireOp",EDGE,"E2.5.2.7"),sQuery(id+"F2.wireOp",EDGE,"E2.5.2.8"),sQuery(id+"F2.wireOp",EDGE,"E2.5.2.9"),sQuery(id+"F2.wireOp",EDGE,"E2.5.2.10"),sQuery(id+"F2.wireOp",EDGE,"E2.5.2.11"),sQuery(id+"F2.wireOp",EDGE,"E2.5.2.13"),sQuery(id+"F2.wireOp",EDGE,"E2.5.3.1"),sQuery(id+"F2.wireOp",EDGE,"E2.5.3.2"),sQuery(id+"F2.wireOp",EDGE,"E2.5.3.3"),sQuery(id+"F2.wireOp",EDGE,"E2.5.3.4"),sQuery(id+"F2.wireOp",EDGE,"E2.5.3.5"),sQuery(id+"F2.wireOp",EDGE,"E2.5.3.10"),sQuery(id+"F2.wireOp",EDGE,"E2.5.3.11"),sQuery(id+"F2.wireOp",EDGE,"E2.5.3.13"),sQuery(id+"F2.wireOp",EDGE,"E2.6.0.7"),sQuery(id+"F2.wireOp",EDGE,"E2.6.0.8"),sQuery(id+"F2.wireOp",EDGE,"E2.6.1.2"),sQuery(id+"F2.wireOp",EDGE,"E2.6.1.3"),sQuery(id+"F2.wireOp",EDGE,"E2.6.1.4"),sQuery(id+"F2.wireOp",EDGE,"E2.6.1.7"),sQuery(id+"F2.wireOp",EDGE,"E2.6.1.8"),sQuery(id+"F2.wireOp",EDGE,"E2.6.1.9"),sQuery(id+"F2.wireOp",EDGE,"E2.6.1.10"),sQuery(id+"F2.wireOp",EDGE,"E2.6.1.11"),sQuery(id+"F2.wireOp",EDGE,"E2.6.2.2"),sQuery(id+"F2.wireOp",EDGE,"E2.6.2.3"),sQuery(id+"F2.wireOp",EDGE,"E2.6.2.4"),sQuery(id+"F2.wireOp",EDGE,"E2.6.2.7"),sQuery(id+"F2.wireOp",EDGE,"E2.6.2.8"),sQuery(id+"F2.wireOp",EDGE,"E2.6.2.9"),sQuery(id+"F2.wireOp",EDGE,"E2.6.2.10"),sQuery(id+"F2.wireOp",EDGE,"E2.6.2.11"),sQuery(id+"F2.wireOp",EDGE,"E2.6.3.2"),sQuery(id+"F2.wireOp",EDGE,"E2.6.3.3"),sQuery(id+"F2.wireOp",EDGE,"E2.6.3.4"),sQuery(id+"F2.wireOp",EDGE,"E2.6.3.10"),sQuery(id+"F2.wireOp",EDGE,"E2.6.3.11"),sQuery(id+"F2.wireOp",EDGE,"E3.0"),sQuery(id+"F2.wireOp",EDGE,"E3.1"),sQuery(id+"F2.wireOp",EDGE,"E3.2"),sQuery(id+"F2.wireOp",EDGE,"E3.3"),sQuery(id+"F2.wireOp",EDGE,"E4.trimOffspring"),sQuery(id+"F2.wireOp",EDGE,"E5.trimOffspring"),sQuery(id+"F2.wireOp",EDGE,"E6.trimOffspring"),sQuery(id+"F2.wireOp",EDGE,"E7.trimOffspring"),sQuery(id+"F2.wireOp",EDGE,"E8.trimOffspring"),sQuery(id+"F2.wireOp",EDGE,"E9.trimOffspring"),sQuery(id+"F2.wireOp",EDGE,"E10.trimOffspring"),sQuery(id+"F2.wireOp",EDGE,"E11.trimOffspring"),sQuery(id+"F2.wireOp",EDGE,"E12.trimOffspring"),sQuery(id+"F2.wireOp",EDGE,"E13.trimOffspring"),sQuery(id+"F2.wireOp",EDGE,"E14.trimOffspring"),sQuery(id+"F2.wireOp",EDGE,"E15.trimOffspring"),sQuery(id+"F2.wireOp",EDGE,"E16.trimOffspring"),sQuery(id+"F2.wireOp",EDGE,"E17.trimOffspring"),sQuery(id+"F2.wireOp",EDGE,"E18.trimOffspring"),sQuery(id+"F2.wireOp",EDGE,"E19.trimOffspring"),sQuery(id+"F2.wireOp",EDGE,"E20.trimOffspring"),sQuery(id+"F2.wireOp",EDGE,"E21.trimOffspring"),sQuery(id+"F2.wireOp",EDGE,"E22.trimOffspring"),sQuery(id+"F2.wireOp",EDGE,"E23.trimOffspring"),sQuery(id+"F2.wireOp",EDGE,"E24.trimOffspring"),sQuery(id+"F2.wireOp",EDGE,"E25.trimOffspring"),sQuery(id+"F2.wireOp",EDGE,"E26.0"),sQuery(id+"F2.wireOp",EDGE,"E26.1"),sQuery(id+"F2.wireOp",EDGE,"E26.2"),sQuery(id+"F2.wireOp",EDGE,"E26.3")])],"isStart":false})]});
            extrude(context, id + "F5", {"entities" : qUnion([Q0]), "operationType" : NewBodyOperationType.ADD, "endBound" : BoundingType.UP_TO_SURFACE, "endBoundEntityFace" : qUnion([Q1]), "depth" : 4 * mm});
        }
        {
            var Q0;
            Q0=qCreatedBy(makeId("Top.planeOp"),FACE);
            var sketch = newSketch(context, id + "F6", { "sketchPlane" : qUnion([Q0])});
            skCircle(sketch, "E33.cCircle", {"center": v(72, 0) * mm, "radius": 11.55 * mm, "construction": true});
            skLineSegment(sketch, "E33.0", {"start": v(72, -11.55) * mm, "end": v(62, -5.77) * mm});
            skLineSegment(sketch, "E33.1", {"start": v(62, -5.77) * mm, "end": v(62, 5.77) * mm});
            skLineSegment(sketch, "E33.2", {"start": v(62, 5.77) * mm, "end": v(72, 11.55) * mm});
            skLineSegment(sketch, "E34.0", {"start": v(70, -35.22) * mm, "end": v(70, 35.22) * mm});
            skSolve(sketch);
        }
        {
            var Q0;
            Q0=qSketchRegion(id+"F6",true);
            var Q1;
            {var subQ0=sQuery(id+"F4.wireOp",EDGE,"E29.0");Q1=makeQuery(id+"F5.boolean.opBoolean","MERGE",FACE,{"derivedFrom":[makeQuery(id+"F3.boolean.opBoolean","MERGE",FACE,{"derivedFrom":[makeQuery(id+"F1.opExtrude","CAP_FACE",FACE,{"disambiguationData":[OSD([sQuery(id+"F0.wireOp",EDGE,"E0.bottom"),sQuery(id+"F0.wireOp",EDGE,"E0.top"),sQuery(id+"F0.wireOp",EDGE,"E0.left"),sQuery(id+"F0.wireOp",EDGE,"E0.right"),sQuery(id+"F0.wireOp",EDGE,"E1.0"),sQuery(id+"F0.wireOp",EDGE,"E1.1"),sQuery(id+"F0.wireOp",EDGE,"E1.2"),sQuery(id+"F0.wireOp",EDGE,"E1.3")])],"isStart":false}),makeQuery(id+"F3.opExtrude","CAP_FACE",FACE,{"disambiguationData":[OSD([sQuery(id+"F2.wireOp",EDGE,"E2.0.1.1"),sQuery(id+"F2.wireOp",EDGE,"E2.0.1.5"),sQuery(id+"F2.wireOp",EDGE,"E2.0.1.13"),sQuery(id+"F2.wireOp",EDGE,"E2.0.2.1"),sQuery(id+"F2.wireOp",EDGE,"E2.0.2.5"),sQuery(id+"F2.wireOp",EDGE,"E2.0.2.13"),sQuery(id+"F2.wireOp",EDGE,"E2.0.3.1"),sQuery(id+"F2.wireOp",EDGE,"E2.0.3.5"),sQuery(id+"F2.wireOp",EDGE,"E2.0.3.13"),sQuery(id+"F2.wireOp",EDGE,"E2.1.0.7"),sQuery(id+"F2.wireOp",EDGE,"E2.1.0.8"),sQuery(id+"F2.wireOp",EDGE,"E2.1.1.1"),sQuery(id+"F2.wireOp",EDGE,"E2.1.1.2"),sQuery(id+"F2.wireOp",EDGE,"E2.1.1.3"),sQuery(id+"F2.wireOp",EDGE,"E2.1.1.4"),sQuery(id+"F2.wireOp",EDGE,"E2.1.1.5"),sQuery(id+"F2.wireOp",EDGE,"E2.1.1.6"),sQuery(id+"F2.wireOp",EDGE,"E2.1.1.7"),sQuery(id+"F2.wireOp",EDGE,"E2.1.1.8"),sQuery(id+"F2.wireOp",EDGE,"E2.1.1.10"),sQuery(id+"F2.wireOp",EDGE,"E2.1.1.11"),sQuery(id+"F2.wireOp",EDGE,"E2.1.1.13"),sQuery(id+"F2.wireOp",EDGE,"E2.1.2.1"),sQuery(id+"F2.wireOp",EDGE,"E2.1.2.2"),sQuery(id+"F2.wireOp",EDGE,"E2.1.2.3"),sQuery(id+"F2.wireOp",EDGE,"E2.1.2.4"),sQuery(id+"F2.wireOp",EDGE,"E2.1.2.5"),sQuery(id+"F2.wireOp",EDGE,"E2.1.2.6"),sQuery(id+"F2.wireOp",EDGE,"E2.1.2.7"),sQuery(id+"F2.wireOp",EDGE,"E2.1.2.8"),sQuery(id+"F2.wireOp",EDGE,"E2.1.2.10"),sQuery(id+"F2.wireOp",EDGE,"E2.1.2.11"),sQuery(id+"F2.wireOp",EDGE,"E2.1.2.13"),sQuery(id+"F2.wireOp",EDGE,"E2.1.3.1"),sQuery(id+"F2.wireOp",EDGE,"E2.1.3.2"),sQuery(id+"F2.wireOp",EDGE,"E2.1.3.3"),sQuery(id+"F2.wireOp",EDGE,"E2.1.3.4"),sQuery(id+"F2.wireOp",EDGE,"E2.1.3.5"),sQuery(id+"F2.wireOp",EDGE,"E2.1.3.10"),sQuery(id+"F2.wireOp",EDGE,"E2.1.3.11"),sQuery(id+"F2.wireOp",EDGE,"E2.1.3.13"),sQuery(id+"F2.wireOp",EDGE,"E2.2.0.7"),sQuery(id+"F2.wireOp",EDGE,"E2.2.0.8"),sQuery(id+"F2.wireOp",EDGE,"E2.2.1.1"),sQuery(id+"F2.wireOp",EDGE,"E2.2.1.2"),sQuery(id+"F2.wireOp",EDGE,"E2.2.1.3"),sQuery(id+"F2.wireOp",EDGE,"E2.2.1.4"),sQuery(id+"F2.wireOp",EDGE,"E2.2.1.5"),sQuery(id+"F2.wireOp",EDGE,"E2.2.1.6"),sQuery(id+"F2.wireOp",EDGE,"E2.2.1.7"),sQuery(id+"F2.wireOp",EDGE,"E2.2.1.8"),sQuery(id+"F2.wireOp",EDGE,"E2.2.1.9"),sQuery(id+"F2.wireOp",EDGE,"E2.2.1.10"),sQuery(id+"F2.wireOp",EDGE,"E2.2.1.11"),sQuery(id+"F2.wireOp",EDGE,"E2.2.1.13"),sQuery(id+"F2.wireOp",EDGE,"E2.2.2.1"),sQuery(id+"F2.wireOp",EDGE,"E2.2.2.2"),sQuery(id+"F2.wireOp",EDGE,"E2.2.2.3"),sQuery(id+"F2.wireOp",EDGE,"E2.2.2.4"),sQuery(id+"F2.wireOp",EDGE,"E2.2.2.5"),sQuery(id+"F2.wireOp",EDGE,"E2.2.2.6"),sQuery(id+"F2.wireOp",EDGE,"E2.2.2.7"),sQuery(id+"F2.wireOp",EDGE,"E2.2.2.8"),sQuery(id+"F2.wireOp",EDGE,"E2.2.2.9"),sQuery(id+"F2.wireOp",EDGE,"E2.2.2.10"),sQuery(id+"F2.wireOp",EDGE,"E2.2.2.11"),sQuery(id+"F2.wireOp",EDGE,"E2.2.2.13"),sQuery(id+"F2.wireOp",EDGE,"E2.2.3.1"),sQuery(id+"F2.wireOp",EDGE,"E2.2.3.2"),sQuery(id+"F2.wireOp",EDGE,"E2.2.3.3"),sQuery(id+"F2.wireOp",EDGE,"E2.2.3.4"),sQuery(id+"F2.wireOp",EDGE,"E2.2.3.5"),sQuery(id+"F2.wireOp",EDGE,"E2.2.3.10"),sQuery(id+"F2.wireOp",EDGE,"E2.2.3.11"),sQuery(id+"F2.wireOp",EDGE,"E2.2.3.13"),sQuery(id+"F2.wireOp",EDGE,"E2.3.0.7"),sQuery(id+"F2.wireOp",EDGE,"E2.3.0.8"),sQuery(id+"F2.wireOp",EDGE,"E2.3.1.1"),sQuery(id+"F2.wireOp",EDGE,"E2.3.1.2"),sQuery(id+"F2.wireOp",EDGE,"E2.3.1.3"),sQuery(id+"F2.wireOp",EDGE,"E2.3.1.4"),sQuery(id+"F2.wireOp",EDGE,"E2.3.1.5"),sQuery(id+"F2.wireOp",EDGE,"E2.3.1.6"),sQuery(id+"F2.wireOp",EDGE,"E2.3.1.7"),sQuery(id+"F2.wireOp",EDGE,"E2.3.1.8"),sQuery(id+"F2.wireOp",EDGE,"E2.3.1.9"),sQuery(id+"F2.wireOp",EDGE,"E2.3.1.10"),sQuery(id+"F2.wireOp",EDGE,"E2.3.1.11"),sQuery(id+"F2.wireOp",EDGE,"E2.3.1.13"),sQuery(id+"F2.wireOp",EDGE,"E2.3.2.1"),sQuery(id+"F2.wireOp",EDGE,"E2.3.2.2"),sQuery(id+"F2.wireOp",EDGE,"E2.3.2.3"),sQuery(id+"F2.wireOp",EDGE,"E2.3.2.4"),sQuery(id+"F2.wireOp",EDGE,"E2.3.2.5"),sQuery(id+"F2.wireOp",EDGE,"E2.3.2.6"),sQuery(id+"F2.wireOp",EDGE,"E2.3.2.7"),sQuery(id+"F2.wireOp",EDGE,"E2.3.2.8"),sQuery(id+"F2.wireOp",EDGE,"E2.3.2.9"),sQuery(id+"F2.wireOp",EDGE,"E2.3.2.10"),sQuery(id+"F2.wireOp",EDGE,"E2.3.2.11"),sQuery(id+"F2.wireOp",EDGE,"E2.3.2.13"),sQuery(id+"F2.wireOp",EDGE,"E2.3.3.1"),sQuery(id+"F2.wireOp",EDGE,"E2.3.3.2"),sQuery(id+"F2.wireOp",EDGE,"E2.3.3.3"),sQuery(id+"F2.wireOp",EDGE,"E2.3.3.4"),sQuery(id+"F2.wireOp",EDGE,"E2.3.3.5"),sQuery(id+"F2.wireOp",EDGE,"E2.3.3.10"),sQuery(id+"F2.wireOp",EDGE,"E2.3.3.11"),sQuery(id+"F2.wireOp",EDGE,"E2.3.3.13"),sQuery(id+"F2.wireOp",EDGE,"E2.4.0.7"),sQuery(id+"F2.wireOp",EDGE,"E2.4.0.8"),sQuery(id+"F2.wireOp",EDGE,"E2.4.1.1"),sQuery(id+"F2.wireOp",EDGE,"E2.4.1.2"),sQuery(id+"F2.wireOp",EDGE,"E2.4.1.3"),sQuery(id+"F2.wireOp",EDGE,"E2.4.1.4"),sQuery(id+"F2.wireOp",EDGE,"E2.4.1.5"),sQuery(id+"F2.wireOp",EDGE,"E2.4.1.6"),sQuery(id+"F2.wireOp",EDGE,"E2.4.1.7"),sQuery(id+"F2.wireOp",EDGE,"E2.4.1.8"),sQuery(id+"F2.wireOp",EDGE,"E2.4.1.9"),sQuery(id+"F2.wireOp",EDGE,"E2.4.1.10"),sQuery(id+"F2.wireOp",EDGE,"E2.4.1.11"),sQuery(id+"F2.wireOp",EDGE,"E2.4.1.13"),sQuery(id+"F2.wireOp",EDGE,"E2.4.2.1"),sQuery(id+"F2.wireOp",EDGE,"E2.4.2.2"),sQuery(id+"F2.wireOp",EDGE,"E2.4.2.3"),sQuery(id+"F2.wireOp",EDGE,"E2.4.2.4"),sQuery(id+"F2.wireOp",EDGE,"E2.4.2.5"),sQuery(id+"F2.wireOp",EDGE,"E2.4.2.6"),sQuery(id+"F2.wireOp",EDGE,"E2.4.2.7"),sQuery(id+"F2.wireOp",EDGE,"E2.4.2.8"),sQuery(id+"F2.wireOp",EDGE,"E2.4.2.9"),sQuery(id+"F2.wireOp",EDGE,"E2.4.2.10"),sQuery(id+"F2.wireOp",EDGE,"E2.4.2.11"),sQuery(id+"F2.wireOp",EDGE,"E2.4.2.13"),sQuery(id+"F2.wireOp",EDGE,"E2.4.3.1"),sQuery(id+"F2.wireOp",EDGE,"E2.4.3.2"),sQuery(id+"F2.wireOp",EDGE,"E2.4.3.3"),sQuery(id+"F2.wireOp",EDGE,"E2.4.3.4"),sQuery(id+"F2.wireOp",EDGE,"E2.4.3.5"),sQuery(id+"F2.wireOp",EDGE,"E2.4.3.10"),sQuery(id+"F2.wireOp",EDGE,"E2.4.3.11"),sQuery(id+"F2.wireOp",EDGE,"E2.4.3.13"),sQuery(id+"F2.wireOp",EDGE,"E2.5.0.7"),sQuery(id+"F2.wireOp",EDGE,"E2.5.0.8"),sQuery(id+"F2.wireOp",EDGE,"E2.5.1.1"),sQuery(id+"F2.wireOp",EDGE,"E2.5.1.2"),sQuery(id+"F2.wireOp",EDGE,"E2.5.1.3"),sQuery(id+"F2.wireOp",EDGE,"E2.5.1.4"),sQuery(id+"F2.wireOp",EDGE,"E2.5.1.5"),sQuery(id+"F2.wireOp",EDGE,"E2.5.1.6"),sQuery(id+"F2.wireOp",EDGE,"E2.5.1.7"),sQuery(id+"F2.wireOp",EDGE,"E2.5.1.8"),sQuery(id+"F2.wireOp",EDGE,"E2.5.1.9"),sQuery(id+"F2.wireOp",EDGE,"E2.5.1.10"),sQuery(id+"F2.wireOp",EDGE,"E2.5.1.11"),sQuery(id+"F2.wireOp",EDGE,"E2.5.1.13"),sQuery(id+"F2.wireOp",EDGE,"E2.5.2.1"),sQuery(id+"F2.wireOp",EDGE,"E2.5.2.2"),sQuery(id+"F2.wireOp",EDGE,"E2.5.2.3"),sQuery(id+"F2.wireOp",EDGE,"E2.5.2.4"),sQuery(id+"F2.wireOp",EDGE,"E2.5.2.5"),sQuery(id+"F2.wireOp",EDGE,"E2.5.2.6"),sQuery(id+"F2.wireOp",EDGE,"E2.5.2.7"),sQuery(id+"F2.wireOp",EDGE,"E2.5.2.8"),sQuery(id+"F2.wireOp",EDGE,"E2.5.2.9"),sQuery(id+"F2.wireOp",EDGE,"E2.5.2.10"),sQuery(id+"F2.wireOp",EDGE,"E2.5.2.11"),sQuery(id+"F2.wireOp",EDGE,"E2.5.2.13"),sQuery(id+"F2.wireOp",EDGE,"E2.5.3.1"),sQuery(id+"F2.wireOp",EDGE,"E2.5.3.2"),sQuery(id+"F2.wireOp",EDGE,"E2.5.3.3"),sQuery(id+"F2.wireOp",EDGE,"E2.5.3.4"),sQuery(id+"F2.wireOp",EDGE,"E2.5.3.5"),sQuery(id+"F2.wireOp",EDGE,"E2.5.3.10"),sQuery(id+"F2.wireOp",EDGE,"E2.5.3.11"),sQuery(id+"F2.wireOp",EDGE,"E2.5.3.13"),sQuery(id+"F2.wireOp",EDGE,"E2.6.0.7"),sQuery(id+"F2.wireOp",EDGE,"E2.6.0.8"),sQuery(id+"F2.wireOp",EDGE,"E2.6.1.2"),sQuery(id+"F2.wireOp",EDGE,"E2.6.1.3"),sQuery(id+"F2.wireOp",EDGE,"E2.6.1.4"),sQuery(id+"F2.wireOp",EDGE,"E2.6.1.7"),sQuery(id+"F2.wireOp",EDGE,"E2.6.1.8"),sQuery(id+"F2.wireOp",EDGE,"E2.6.1.9"),sQuery(id+"F2.wireOp",EDGE,"E2.6.1.10"),sQuery(id+"F2.wireOp",EDGE,"E2.6.1.11"),sQuery(id+"F2.wireOp",EDGE,"E2.6.2.2"),sQuery(id+"F2.wireOp",EDGE,"E2.6.2.3"),sQuery(id+"F2.wireOp",EDGE,"E2.6.2.4"),sQuery(id+"F2.wireOp",EDGE,"E2.6.2.7"),sQuery(id+"F2.wireOp",EDGE,"E2.6.2.8"),sQuery(id+"F2.wireOp",EDGE,"E2.6.2.9"),sQuery(id+"F2.wireOp",EDGE,"E2.6.2.10"),sQuery(id+"F2.wireOp",EDGE,"E2.6.2.11"),sQuery(id+"F2.wireOp",EDGE,"E2.6.3.2"),sQuery(id+"F2.wireOp",EDGE,"E2.6.3.3"),sQuery(id+"F2.wireOp",EDGE,"E2.6.3.4"),sQuery(id+"F2.wireOp",EDGE,"E2.6.3.10"),sQuery(id+"F2.wireOp",EDGE,"E2.6.3.11"),sQuery(id+"F2.wireOp",EDGE,"E3.0"),sQuery(id+"F2.wireOp",EDGE,"E3.1"),sQuery(id+"F2.wireOp",EDGE,"E3.2"),sQuery(id+"F2.wireOp",EDGE,"E3.3"),sQuery(id+"F2.wireOp",EDGE,"E4.trimOffspring"),sQuery(id+"F2.wireOp",EDGE,"E5.trimOffspring"),sQuery(id+"F2.wireOp",EDGE,"E6.trimOffspring"),sQuery(id+"F2.wireOp",EDGE,"E7.trimOffspring"),sQuery(id+"F2.wireOp",EDGE,"E8.trimOffspring"),sQuery(id+"F2.wireOp",EDGE,"E9.trimOffspring"),sQuery(id+"F2.wireOp",EDGE,"E10.trimOffspring"),sQuery(id+"F2.wireOp",EDGE,"E11.trimOffspring"),sQuery(id+"F2.wireOp",EDGE,"E12.trimOffspring"),sQuery(id+"F2.wireOp",EDGE,"E13.trimOffspring"),sQuery(id+"F2.wireOp",EDGE,"E14.trimOffspring"),sQuery(id+"F2.wireOp",EDGE,"E15.trimOffspring"),sQuery(id+"F2.wireOp",EDGE,"E16.trimOffspring"),sQuery(id+"F2.wireOp",EDGE,"E17.trimOffspring"),sQuery(id+"F2.wireOp",EDGE,"E18.trimOffspring"),sQuery(id+"F2.wireOp",EDGE,"E19.trimOffspring"),sQuery(id+"F2.wireOp",EDGE,"E20.trimOffspring"),sQuery(id+"F2.wireOp",EDGE,"E21.trimOffspring"),sQuery(id+"F2.wireOp",EDGE,"E22.trimOffspring"),sQuery(id+"F2.wireOp",EDGE,"E23.trimOffspring"),sQuery(id+"F2.wireOp",EDGE,"E24.trimOffspring"),sQuery(id+"F2.wireOp",EDGE,"E25.trimOffspring"),sQuery(id+"F2.wireOp",EDGE,"E26.0"),sQuery(id+"F2.wireOp",EDGE,"E26.1"),sQuery(id+"F2.wireOp",EDGE,"E26.2"),sQuery(id+"F2.wireOp",EDGE,"E26.3")])],"isStart":false})]}),makeQuery(id+"F5.opExtrude","CAP_FACE",FACE,{"disambiguationData":[OSD([subQ0,sQuery(id+"F4.wireOp",EDGE,"E32.0"),sQuery(id+"F4.wireOp",EDGE,"E32.1"),sQuery(id+"F4.wireOp",EDGE,"E32.2")])],"isStart":false}),makeQuery(id+"F5.opExtrude","CAP_FACE",FACE,{"disambiguationData":[OSD([subQ0,sQuery(id+"F4.wireOp",EDGE,"E31.0"),sQuery(id+"F4.wireOp",EDGE,"E31.1"),sQuery(id+"F4.wireOp",EDGE,"E31.2")])],"isStart":false})]});}
            extrude(context, id + "F7", {"entities" : qUnion([Q0]), "operationType" : NewBodyOperationType.ADD, "endBound" : BoundingType.UP_TO_SURFACE, "endBoundEntityFace" : qUnion([Q1]), "depth" : 25 * mm});
        }
        {
            var Q0;
            Q0=qCreatedBy(makeId("Top.planeOp"),FACE);
            var sketch = newSketch(context, id + "F8", { "sketchPlane" : qUnion([Q0])});
            skCircle(sketch, "E35.cCircle", {"center": v(-36, 57.74) * mm, "radius": 11.55 * mm, "construction": true});
            skLineSegment(sketch, "E35.0", {"start": v(-36, 46.19) * mm, "end": v(-46, 51.96) * mm});
            skLineSegment(sketch, "E35.1", {"start": v(-46, 51.96) * mm, "end": v(-46, 63.5) * mm, "construction": true});
            skLineSegment(sketch, "E35.2", {"start": v(-46, 63.5) * mm, "end": v(-36, 69.28) * mm, "construction": true});
            skLineSegment(sketch, "E35.3", {"start": v(-36, 69.28) * mm, "end": v(-26, 63.5) * mm, "construction": true});
            skLineSegment(sketch, "E35.4", {"start": v(-26, 63.5) * mm, "end": v(-26, 51.96) * mm, "construction": true});
            skLineSegment(sketch, "E35.5", {"start": v(-26, 51.96) * mm, "end": v(-36, 46.19) * mm});
            skCircle(sketch, "E36.cCircle", {"center": v(36, 57.74) * mm, "radius": 11.55 * mm, "construction": true});
            skLineSegment(sketch, "E36.0", {"start": v(36, 46.19) * mm, "end": v(26, 51.96) * mm});
            skLineSegment(sketch, "E36.1", {"start": v(26, 51.96) * mm, "end": v(26, 63.5) * mm, "construction": true});
            skLineSegment(sketch, "E36.2", {"start": v(26, 63.5) * mm, "end": v(36, 69.28) * mm, "construction": true});
            skLineSegment(sketch, "E36.3", {"start": v(36, 69.28) * mm, "end": v(46, 63.5) * mm, "construction": true});
            skLineSegment(sketch, "E36.4", {"start": v(46, 63.5) * mm, "end": v(46, 51.96) * mm, "construction": true});
            skLineSegment(sketch, "E36.5", {"start": v(46, 51.96) * mm, "end": v(36, 46.19) * mm});
            skCircle(sketch, "E37.cCircle", {"center": v(-36, -57.74) * mm, "radius": 11.55 * mm, "construction": true});
            skLineSegment(sketch, "E37.0", {"start": v(-36, -69.28) * mm, "end": v(-46, -63.5) * mm, "construction": true});
            skLineSegment(sketch, "E37.1", {"start": v(-46, -63.5) * mm, "end": v(-46, -51.96) * mm, "construction": true});
            skLineSegment(sketch, "E37.2", {"start": v(-46, -51.96) * mm, "end": v(-36, -46.19) * mm});
            skLineSegment(sketch, "E37.3", {"start": v(-36, -46.19) * mm, "end": v(-26, -51.96) * mm});
            skLineSegment(sketch, "E37.4", {"start": v(-26, -51.96) * mm, "end": v(-26, -63.5) * mm, "construction": true});
            skLineSegment(sketch, "E37.5", {"start": v(-26, -63.5) * mm, "end": v(-36, -69.28) * mm, "construction": true});
            skCircle(sketch, "E38.cCircle", {"center": v(36, -57.74) * mm, "radius": 11.55 * mm, "construction": true});
            skLineSegment(sketch, "E38.0", {"start": v(26, -63.5) * mm, "end": v(26, -51.96) * mm, "construction": true});
            skLineSegment(sketch, "E38.1", {"start": v(26, -51.96) * mm, "end": v(36, -46.19) * mm});
            skLineSegment(sketch, "E38.2", {"start": v(36, -46.19) * mm, "end": v(46, -51.96) * mm});
            skLineSegment(sketch, "E38.3", {"start": v(46, -51.96) * mm, "end": v(46, -63.5) * mm, "construction": true});
            skLineSegment(sketch, "E38.4", {"start": v(46, -63.5) * mm, "end": v(36, -69.28) * mm, "construction": true});
            skLineSegment(sketch, "E38.5", {"start": v(36, -69.28) * mm, "end": v(26, -63.5) * mm, "construction": true});
            skLineSegment(sketch, "E39.0", {"start": v(-36, 66.63) * mm, "end": v(-24.7, 60.1) * mm});
            skLineSegment(sketch, "E39.1", {"start": v(-47.3, 60.1) * mm, "end": v(-36, 66.63) * mm});
            skLineSegment(sketch, "E40.0", {"start": v(36, 66.63) * mm, "end": v(46.57, 60.52) * mm});
            skLineSegment(sketch, "E40.1", {"start": v(23.52, 59.42) * mm, "end": v(36, 66.63) * mm});
            skLineSegment(sketch, "E41.0", {"start": v(-36, -66.63) * mm, "end": v(-48.85, -59.2) * mm});
            skLineSegment(sketch, "E41.1", {"start": v(-24.7, -60.1) * mm, "end": v(-36, -66.63) * mm});
            skLineSegment(sketch, "E42.0", {"start": v(36, -66.63) * mm, "end": v(23.2, -59.23) * mm});
            skLineSegment(sketch, "E42.1", {"start": v(48.37, -59.48) * mm, "end": v(36, -66.63) * mm});
            skLineSegment(sketch, "E43.0", {"start": v(26.5, -63.5) * mm, "end": v(26.5, -51.96) * mm});
            skLineSegment(sketch, "E44.0", {"start": v(45.5, -51.96) * mm, "end": v(45.5, -63.5) * mm});
            skLineSegment(sketch, "E45.0", {"start": v(-45.5, -63.5) * mm, "end": v(-45.5, -51.96) * mm});
            skLineSegment(sketch, "E46.0", {"start": v(-26.5, -51.96) * mm, "end": v(-26.5, -63.5) * mm});
            skLineSegment(sketch, "E47.0", {"start": v(-45.5, 51.96) * mm, "end": v(-45.5, 63.5) * mm});
            skLineSegment(sketch, "E48.0", {"start": v(-26.5, 63.5) * mm, "end": v(-26.5, 51.96) * mm});
            skLineSegment(sketch, "E49.0", {"start": v(26.5, 51.96) * mm, "end": v(26.5, 63.5) * mm});
            skLineSegment(sketch, "E50.0", {"start": v(45.5, 63.5) * mm, "end": v(45.5, 51.96) * mm});
            skLineSegment(sketch, "E51.0", {"start": v(70, -59) * mm, "end": v(-70, -59) * mm});
            skLineSegment(sketch, "E52.0", {"start": v(70, 59) * mm, "end": v(-70, 59) * mm});
            skSolve(sketch);
        }
        {
            var Q0;
            Q0 = qSketchRegion(id + "F8", true);
            var Q1;
            {var subQ0=sQuery(id+"F4.wireOp",EDGE,"E29.0");Q1=makeQuery(id+"F5.boolean.opBoolean","MERGE",FACE,{"derivedFrom":[makeQuery(id+"F3.boolean.opBoolean","MERGE",FACE,{"derivedFrom":[makeQuery(id+"F1.opExtrude","CAP_FACE",FACE,{"disambiguationData":[OSD([sQuery(id+"F0.wireOp",EDGE,"E0.bottom"),sQuery(id+"F0.wireOp",EDGE,"E0.top"),sQuery(id+"F0.wireOp",EDGE,"E0.left"),sQuery(id+"F0.wireOp",EDGE,"E0.right"),sQuery(id+"F0.wireOp",EDGE,"E1.0"),sQuery(id+"F0.wireOp",EDGE,"E1.1"),sQuery(id+"F0.wireOp",EDGE,"E1.2"),sQuery(id+"F0.wireOp",EDGE,"E1.3")])],"isStart":false}),makeQuery(id+"F3.opExtrude","CAP_FACE",FACE,{"disambiguationData":[OSD([sQuery(id+"F2.wireOp",EDGE,"E2.0.1.1"),sQuery(id+"F2.wireOp",EDGE,"E2.0.1.5"),sQuery(id+"F2.wireOp",EDGE,"E2.0.1.13"),sQuery(id+"F2.wireOp",EDGE,"E2.0.2.1"),sQuery(id+"F2.wireOp",EDGE,"E2.0.2.5"),sQuery(id+"F2.wireOp",EDGE,"E2.0.2.13"),sQuery(id+"F2.wireOp",EDGE,"E2.0.3.1"),sQuery(id+"F2.wireOp",EDGE,"E2.0.3.5"),sQuery(id+"F2.wireOp",EDGE,"E2.0.3.13"),sQuery(id+"F2.wireOp",EDGE,"E2.1.0.7"),sQuery(id+"F2.wireOp",EDGE,"E2.1.0.8"),sQuery(id+"F2.wireOp",EDGE,"E2.1.1.1"),sQuery(id+"F2.wireOp",EDGE,"E2.1.1.2"),sQuery(id+"F2.wireOp",EDGE,"E2.1.1.3"),sQuery(id+"F2.wireOp",EDGE,"E2.1.1.4"),sQuery(id+"F2.wireOp",EDGE,"E2.1.1.5"),sQuery(id+"F2.wireOp",EDGE,"E2.1.1.6"),sQuery(id+"F2.wireOp",EDGE,"E2.1.1.7"),sQuery(id+"F2.wireOp",EDGE,"E2.1.1.8"),sQuery(id+"F2.wireOp",EDGE,"E2.1.1.10"),sQuery(id+"F2.wireOp",EDGE,"E2.1.1.11"),sQuery(id+"F2.wireOp",EDGE,"E2.1.1.13"),sQuery(id+"F2.wireOp",EDGE,"E2.1.2.1"),sQuery(id+"F2.wireOp",EDGE,"E2.1.2.2"),sQuery(id+"F2.wireOp",EDGE,"E2.1.2.3"),sQuery(id+"F2.wireOp",EDGE,"E2.1.2.4"),sQuery(id+"F2.wireOp",EDGE,"E2.1.2.5"),sQuery(id+"F2.wireOp",EDGE,"E2.1.2.6"),sQuery(id+"F2.wireOp",EDGE,"E2.1.2.7"),sQuery(id+"F2.wireOp",EDGE,"E2.1.2.8"),sQuery(id+"F2.wireOp",EDGE,"E2.1.2.10"),sQuery(id+"F2.wireOp",EDGE,"E2.1.2.11"),sQuery(id+"F2.wireOp",EDGE,"E2.1.2.13"),sQuery(id+"F2.wireOp",EDGE,"E2.1.3.1"),sQuery(id+"F2.wireOp",EDGE,"E2.1.3.2"),sQuery(id+"F2.wireOp",EDGE,"E2.1.3.3"),sQuery(id+"F2.wireOp",EDGE,"E2.1.3.4"),sQuery(id+"F2.wireOp",EDGE,"E2.1.3.5"),sQuery(id+"F2.wireOp",EDGE,"E2.1.3.10"),sQuery(id+"F2.wireOp",EDGE,"E2.1.3.11"),sQuery(id+"F2.wireOp",EDGE,"E2.1.3.13"),sQuery(id+"F2.wireOp",EDGE,"E2.2.0.7"),sQuery(id+"F2.wireOp",EDGE,"E2.2.0.8"),sQuery(id+"F2.wireOp",EDGE,"E2.2.1.1"),sQuery(id+"F2.wireOp",EDGE,"E2.2.1.2"),sQuery(id+"F2.wireOp",EDGE,"E2.2.1.3"),sQuery(id+"F2.wireOp",EDGE,"E2.2.1.4"),sQuery(id+"F2.wireOp",EDGE,"E2.2.1.5"),sQuery(id+"F2.wireOp",EDGE,"E2.2.1.6"),sQuery(id+"F2.wireOp",EDGE,"E2.2.1.7"),sQuery(id+"F2.wireOp",EDGE,"E2.2.1.8"),sQuery(id+"F2.wireOp",EDGE,"E2.2.1.9"),sQuery(id+"F2.wireOp",EDGE,"E2.2.1.10"),sQuery(id+"F2.wireOp",EDGE,"E2.2.1.11"),sQuery(id+"F2.wireOp",EDGE,"E2.2.1.13"),sQuery(id+"F2.wireOp",EDGE,"E2.2.2.1"),sQuery(id+"F2.wireOp",EDGE,"E2.2.2.2"),sQuery(id+"F2.wireOp",EDGE,"E2.2.2.3"),sQuery(id+"F2.wireOp",EDGE,"E2.2.2.4"),sQuery(id+"F2.wireOp",EDGE,"E2.2.2.5"),sQuery(id+"F2.wireOp",EDGE,"E2.2.2.6"),sQuery(id+"F2.wireOp",EDGE,"E2.2.2.7"),sQuery(id+"F2.wireOp",EDGE,"E2.2.2.8"),sQuery(id+"F2.wireOp",EDGE,"E2.2.2.9"),sQuery(id+"F2.wireOp",EDGE,"E2.2.2.10"),sQuery(id+"F2.wireOp",EDGE,"E2.2.2.11"),sQuery(id+"F2.wireOp",EDGE,"E2.2.2.13"),sQuery(id+"F2.wireOp",EDGE,"E2.2.3.1"),sQuery(id+"F2.wireOp",EDGE,"E2.2.3.2"),sQuery(id+"F2.wireOp",EDGE,"E2.2.3.3"),sQuery(id+"F2.wireOp",EDGE,"E2.2.3.4"),sQuery(id+"F2.wireOp",EDGE,"E2.2.3.5"),sQuery(id+"F2.wireOp",EDGE,"E2.2.3.10"),sQuery(id+"F2.wireOp",EDGE,"E2.2.3.11"),sQuery(id+"F2.wireOp",EDGE,"E2.2.3.13"),sQuery(id+"F2.wireOp",EDGE,"E2.3.0.7"),sQuery(id+"F2.wireOp",EDGE,"E2.3.0.8"),sQuery(id+"F2.wireOp",EDGE,"E2.3.1.1"),sQuery(id+"F2.wireOp",EDGE,"E2.3.1.2"),sQuery(id+"F2.wireOp",EDGE,"E2.3.1.3"),sQuery(id+"F2.wireOp",EDGE,"E2.3.1.4"),sQuery(id+"F2.wireOp",EDGE,"E2.3.1.5"),sQuery(id+"F2.wireOp",EDGE,"E2.3.1.6"),sQuery(id+"F2.wireOp",EDGE,"E2.3.1.7"),sQuery(id+"F2.wireOp",EDGE,"E2.3.1.8"),sQuery(id+"F2.wireOp",EDGE,"E2.3.1.9"),sQuery(id+"F2.wireOp",EDGE,"E2.3.1.10"),sQuery(id+"F2.wireOp",EDGE,"E2.3.1.11"),sQuery(id+"F2.wireOp",EDGE,"E2.3.1.13"),sQuery(id+"F2.wireOp",EDGE,"E2.3.2.1"),sQuery(id+"F2.wireOp",EDGE,"E2.3.2.2"),sQuery(id+"F2.wireOp",EDGE,"E2.3.2.3"),sQuery(id+"F2.wireOp",EDGE,"E2.3.2.4"),sQuery(id+"F2.wireOp",EDGE,"E2.3.2.5"),sQuery(id+"F2.wireOp",EDGE,"E2.3.2.6"),sQuery(id+"F2.wireOp",EDGE,"E2.3.2.7"),sQuery(id+"F2.wireOp",EDGE,"E2.3.2.8"),sQuery(id+"F2.wireOp",EDGE,"E2.3.2.9"),sQuery(id+"F2.wireOp",EDGE,"E2.3.2.10"),sQuery(id+"F2.wireOp",EDGE,"E2.3.2.11"),sQuery(id+"F2.wireOp",EDGE,"E2.3.2.13"),sQuery(id+"F2.wireOp",EDGE,"E2.3.3.1"),sQuery(id+"F2.wireOp",EDGE,"E2.3.3.2"),sQuery(id+"F2.wireOp",EDGE,"E2.3.3.3"),sQuery(id+"F2.wireOp",EDGE,"E2.3.3.4"),sQuery(id+"F2.wireOp",EDGE,"E2.3.3.5"),sQuery(id+"F2.wireOp",EDGE,"E2.3.3.10"),sQuery(id+"F2.wireOp",EDGE,"E2.3.3.11"),sQuery(id+"F2.wireOp",EDGE,"E2.3.3.13"),sQuery(id+"F2.wireOp",EDGE,"E2.4.0.7"),sQuery(id+"F2.wireOp",EDGE,"E2.4.0.8"),sQuery(id+"F2.wireOp",EDGE,"E2.4.1.1"),sQuery(id+"F2.wireOp",EDGE,"E2.4.1.2"),sQuery(id+"F2.wireOp",EDGE,"E2.4.1.3"),sQuery(id+"F2.wireOp",EDGE,"E2.4.1.4"),sQuery(id+"F2.wireOp",EDGE,"E2.4.1.5"),sQuery(id+"F2.wireOp",EDGE,"E2.4.1.6"),sQuery(id+"F2.wireOp",EDGE,"E2.4.1.7"),sQuery(id+"F2.wireOp",EDGE,"E2.4.1.8"),sQuery(id+"F2.wireOp",EDGE,"E2.4.1.9"),sQuery(id+"F2.wireOp",EDGE,"E2.4.1.10"),sQuery(id+"F2.wireOp",EDGE,"E2.4.1.11"),sQuery(id+"F2.wireOp",EDGE,"E2.4.1.13"),sQuery(id+"F2.wireOp",EDGE,"E2.4.2.1"),sQuery(id+"F2.wireOp",EDGE,"E2.4.2.2"),sQuery(id+"F2.wireOp",EDGE,"E2.4.2.3"),sQuery(id+"F2.wireOp",EDGE,"E2.4.2.4"),sQuery(id+"F2.wireOp",EDGE,"E2.4.2.5"),sQuery(id+"F2.wireOp",EDGE,"E2.4.2.6"),sQuery(id+"F2.wireOp",EDGE,"E2.4.2.7"),sQuery(id+"F2.wireOp",EDGE,"E2.4.2.8"),sQuery(id+"F2.wireOp",EDGE,"E2.4.2.9"),sQuery(id+"F2.wireOp",EDGE,"E2.4.2.10"),sQuery(id+"F2.wireOp",EDGE,"E2.4.2.11"),sQuery(id+"F2.wireOp",EDGE,"E2.4.2.13"),sQuery(id+"F2.wireOp",EDGE,"E2.4.3.1"),sQuery(id+"F2.wireOp",EDGE,"E2.4.3.2"),sQuery(id+"F2.wireOp",EDGE,"E2.4.3.3"),sQuery(id+"F2.wireOp",EDGE,"E2.4.3.4"),sQuery(id+"F2.wireOp",EDGE,"E2.4.3.5"),sQuery(id+"F2.wireOp",EDGE,"E2.4.3.10"),sQuery(id+"F2.wireOp",EDGE,"E2.4.3.11"),sQuery(id+"F2.wireOp",EDGE,"E2.4.3.13"),sQuery(id+"F2.wireOp",EDGE,"E2.5.0.7"),sQuery(id+"F2.wireOp",EDGE,"E2.5.0.8"),sQuery(id+"F2.wireOp",EDGE,"E2.5.1.1"),sQuery(id+"F2.wireOp",EDGE,"E2.5.1.2"),sQuery(id+"F2.wireOp",EDGE,"E2.5.1.3"),sQuery(id+"F2.wireOp",EDGE,"E2.5.1.4"),sQuery(id+"F2.wireOp",EDGE,"E2.5.1.5"),sQuery(id+"F2.wireOp",EDGE,"E2.5.1.6"),sQuery(id+"F2.wireOp",EDGE,"E2.5.1.7"),sQuery(id+"F2.wireOp",EDGE,"E2.5.1.8"),sQuery(id+"F2.wireOp",EDGE,"E2.5.1.9"),sQuery(id+"F2.wireOp",EDGE,"E2.5.1.10"),sQuery(id+"F2.wireOp",EDGE,"E2.5.1.11"),sQuery(id+"F2.wireOp",EDGE,"E2.5.1.13"),sQuery(id+"F2.wireOp",EDGE,"E2.5.2.1"),sQuery(id+"F2.wireOp",EDGE,"E2.5.2.2"),sQuery(id+"F2.wireOp",EDGE,"E2.5.2.3"),sQuery(id+"F2.wireOp",EDGE,"E2.5.2.4"),sQuery(id+"F2.wireOp",EDGE,"E2.5.2.5"),sQuery(id+"F2.wireOp",EDGE,"E2.5.2.6"),sQuery(id+"F2.wireOp",EDGE,"E2.5.2.7"),sQuery(id+"F2.wireOp",EDGE,"E2.5.2.8"),sQuery(id+"F2.wireOp",EDGE,"E2.5.2.9"),sQuery(id+"F2.wireOp",EDGE,"E2.5.2.10"),sQuery(id+"F2.wireOp",EDGE,"E2.5.2.11"),sQuery(id+"F2.wireOp",EDGE,"E2.5.2.13"),sQuery(id+"F2.wireOp",EDGE,"E2.5.3.1"),sQuery(id+"F2.wireOp",EDGE,"E2.5.3.2"),sQuery(id+"F2.wireOp",EDGE,"E2.5.3.3"),sQuery(id+"F2.wireOp",EDGE,"E2.5.3.4"),sQuery(id+"F2.wireOp",EDGE,"E2.5.3.5"),sQuery(id+"F2.wireOp",EDGE,"E2.5.3.10"),sQuery(id+"F2.wireOp",EDGE,"E2.5.3.11"),sQuery(id+"F2.wireOp",EDGE,"E2.5.3.13"),sQuery(id+"F2.wireOp",EDGE,"E2.6.0.7"),sQuery(id+"F2.wireOp",EDGE,"E2.6.0.8"),sQuery(id+"F2.wireOp",EDGE,"E2.6.1.2"),sQuery(id+"F2.wireOp",EDGE,"E2.6.1.3"),sQuery(id+"F2.wireOp",EDGE,"E2.6.1.4"),sQuery(id+"F2.wireOp",EDGE,"E2.6.1.7"),sQuery(id+"F2.wireOp",EDGE,"E2.6.1.8"),sQuery(id+"F2.wireOp",EDGE,"E2.6.1.9"),sQuery(id+"F2.wireOp",EDGE,"E2.6.1.10"),sQuery(id+"F2.wireOp",EDGE,"E2.6.1.11"),sQuery(id+"F2.wireOp",EDGE,"E2.6.2.2"),sQuery(id+"F2.wireOp",EDGE,"E2.6.2.3"),sQuery(id+"F2.wireOp",EDGE,"E2.6.2.4"),sQuery(id+"F2.wireOp",EDGE,"E2.6.2.7"),sQuery(id+"F2.wireOp",EDGE,"E2.6.2.8"),sQuery(id+"F2.wireOp",EDGE,"E2.6.2.9"),sQuery(id+"F2.wireOp",EDGE,"E2.6.2.10"),sQuery(id+"F2.wireOp",EDGE,"E2.6.2.11"),sQuery(id+"F2.wireOp",EDGE,"E2.6.3.2"),sQuery(id+"F2.wireOp",EDGE,"E2.6.3.3"),sQuery(id+"F2.wireOp",EDGE,"E2.6.3.4"),sQuery(id+"F2.wireOp",EDGE,"E2.6.3.10"),sQuery(id+"F2.wireOp",EDGE,"E2.6.3.11"),sQuery(id+"F2.wireOp",EDGE,"E3.0"),sQuery(id+"F2.wireOp",EDGE,"E3.1"),sQuery(id+"F2.wireOp",EDGE,"E3.2"),sQuery(id+"F2.wireOp",EDGE,"E3.3"),sQuery(id+"F2.wireOp",EDGE,"E4.trimOffspring"),sQuery(id+"F2.wireOp",EDGE,"E5.trimOffspring"),sQuery(id+"F2.wireOp",EDGE,"E6.trimOffspring"),sQuery(id+"F2.wireOp",EDGE,"E7.trimOffspring"),sQuery(id+"F2.wireOp",EDGE,"E8.trimOffspring"),sQuery(id+"F2.wireOp",EDGE,"E9.trimOffspring"),sQuery(id+"F2.wireOp",EDGE,"E10.trimOffspring"),sQuery(id+"F2.wireOp",EDGE,"E11.trimOffspring"),sQuery(id+"F2.wireOp",EDGE,"E12.trimOffspring"),sQuery(id+"F2.wireOp",EDGE,"E13.trimOffspring"),sQuery(id+"F2.wireOp",EDGE,"E14.trimOffspring"),sQuery(id+"F2.wireOp",EDGE,"E15.trimOffspring"),sQuery(id+"F2.wireOp",EDGE,"E16.trimOffspring"),sQuery(id+"F2.wireOp",EDGE,"E17.trimOffspring"),sQuery(id+"F2.wireOp",EDGE,"E18.trimOffspring"),sQuery(id+"F2.wireOp",EDGE,"E19.trimOffspring"),sQuery(id+"F2.wireOp",EDGE,"E20.trimOffspring"),sQuery(id+"F2.wireOp",EDGE,"E21.trimOffspring"),sQuery(id+"F2.wireOp",EDGE,"E22.trimOffspring"),sQuery(id+"F2.wireOp",EDGE,"E23.trimOffspring"),sQuery(id+"F2.wireOp",EDGE,"E24.trimOffspring"),sQuery(id+"F2.wireOp",EDGE,"E25.trimOffspring"),sQuery(id+"F2.wireOp",EDGE,"E26.0"),sQuery(id+"F2.wireOp",EDGE,"E26.1"),sQuery(id+"F2.wireOp",EDGE,"E26.2"),sQuery(id+"F2.wireOp",EDGE,"E26.3")])],"isStart":false})]}),makeQuery(id+"F5.opExtrude","CAP_FACE",FACE,{"disambiguationData":[OSD([subQ0,sQuery(id+"F4.wireOp",EDGE,"E32.0"),sQuery(id+"F4.wireOp",EDGE,"E32.1"),sQuery(id+"F4.wireOp",EDGE,"E32.2")])],"isStart":false}),makeQuery(id+"F5.opExtrude","CAP_FACE",FACE,{"disambiguationData":[OSD([subQ0,sQuery(id+"F4.wireOp",EDGE,"E31.0"),sQuery(id+"F4.wireOp",EDGE,"E31.1"),sQuery(id+"F4.wireOp",EDGE,"E31.2")])],"isStart":false})]});}
            extrude(context, id + "F9", {"entities" : qUnion([Q0]), "operationType" : NewBodyOperationType.ADD, "endBound" : BoundingType.UP_TO_SURFACE, "endBoundEntityFace" : qUnion([Q1]), "depth" : 25 * mm});
        }
        {
            var Q0;
            Q0=qCreatedBy(makeId("Top.planeOp"),FACE);
            var sketch = newSketch(context, id + "F10", { "sketchPlane" : qUnion([Q0])});
            skLineSegment(sketch, "E53.0", {"start": v(62, -5.77) * mm, "end": v(62, 5.77) * mm, "construction": true});
            skLineSegment(sketch, "E53.1", {"start": v(62, 5.77) * mm, "end": v(66, 8.08) * mm, "construction": true});
            skLineSegment(sketch, "E53.2", {"start": v(66, -8.08) * mm, "end": v(62, -5.77) * mm, "construction": true});
            skLineSegment(sketch, "E54.0", {"start": v(70, -35.22) * mm, "end": v(70, 35.22) * mm});
            skCircle(sketch, "E55.cCircle", {"center": v(72, 0) * mm, "radius": 11.55 * mm, "construction": true});
            skLineSegment(sketch, "E55.0", {"start": v(72, -11.55) * mm, "end": v(62, -5.77) * mm, "construction": true});
            skLineSegment(sketch, "E55.2", {"start": v(62, 5.77) * mm, "end": v(72, 11.55) * mm, "construction": true});
            skLineSegment(sketch, "E55.3", {"start": v(72, 11.55) * mm, "end": v(82, 5.77) * mm, "construction": true});
            skLineSegment(sketch, "E55.4", {"start": v(82, 5.77) * mm, "end": v(82, -5.77) * mm, "construction": true});
            skLineSegment(sketch, "E55.5", {"start": v(82, -5.77) * mm, "end": v(72, -11.55) * mm, "construction": true});
            skLineSegment(sketch, "E56.0", {"start": v(65, 4.04) * mm, "end": v(73.5, 8.95) * mm});
            skLineSegment(sketch, "E56.1", {"start": v(65, -4.04) * mm, "end": v(65, 4.04) * mm});
            skLineSegment(sketch, "E56.2", {"start": v(73.5, -8.95) * mm, "end": v(65, -4.04) * mm});
            skSolve(sketch);
        }
        {
            var Q0;
            Q0 = qSketchRegion(id + "F10", true);
            extrude(context, id + "F11", {"entities" : qUnion([Q0]), "operationType" : NewBodyOperationType.REMOVE, "endBound" : BoundingType.THROUGH_ALL, "depth" : 25 * mm});
        }
    });
